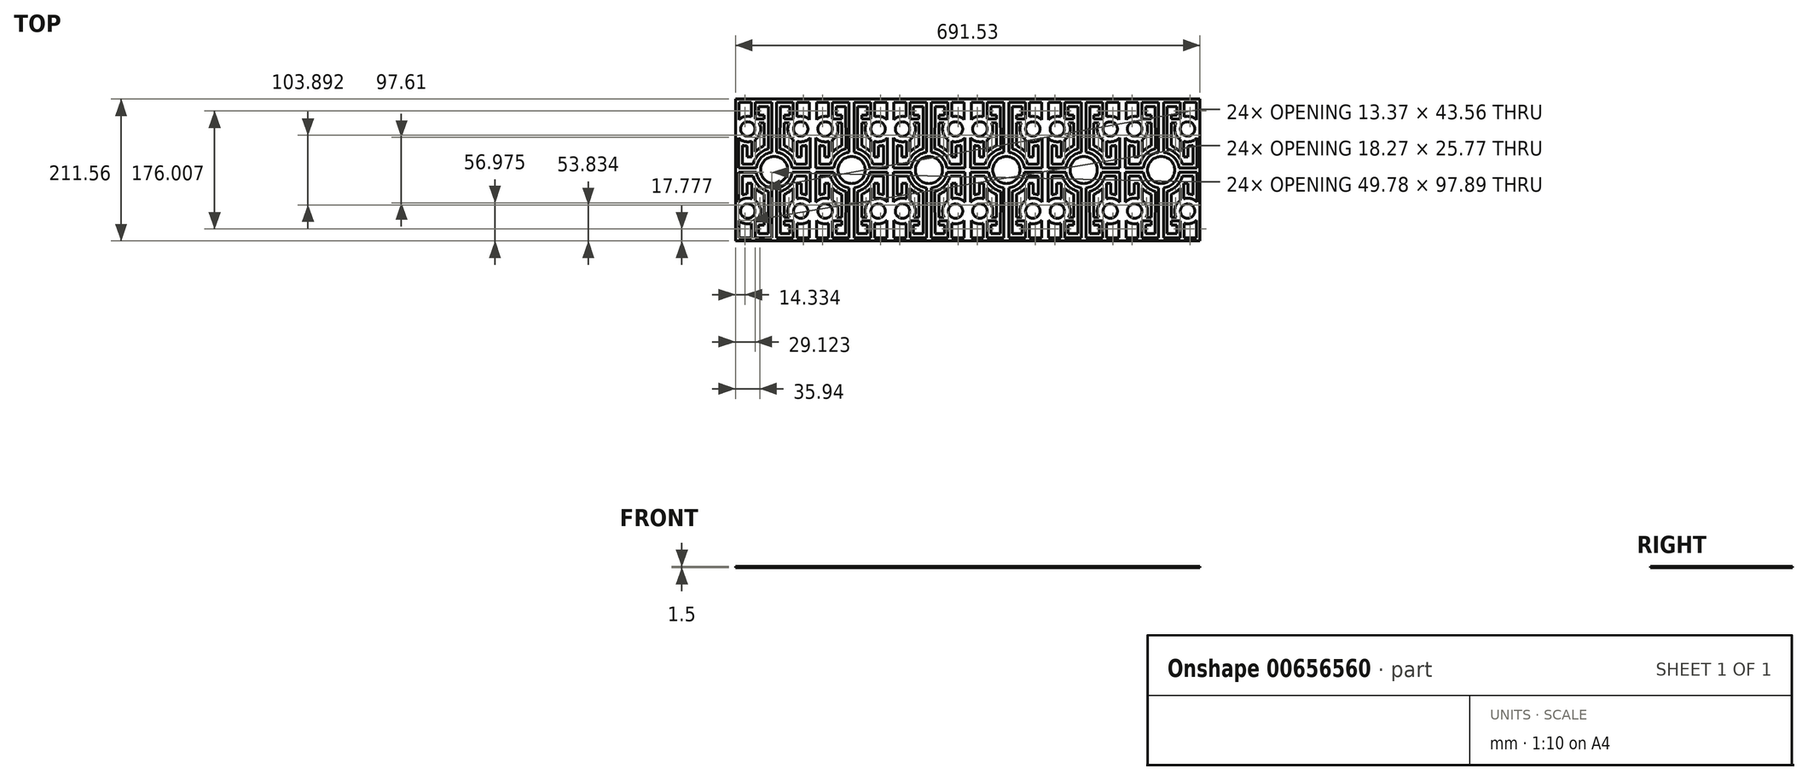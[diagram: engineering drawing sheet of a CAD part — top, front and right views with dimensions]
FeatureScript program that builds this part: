
annotation { "Feature Type Name" : "Feature", "Feature Type Description" : "" }
export const myFeature = defineFeature(function(context is Context, id is Id, definition is map)
    precondition{}
    {
        {
            var Q0;
            Q0=qCreatedBy(makeId("Top.planeOp"),FACE);
            var sketch = newSketch(context, id + "F0", { "sketchPlane" : qUnion([Q0])});
            skLineSegment(sketch, "E0.bottom", {"start": v(57.63, -105.78) * mm, "end": v(-57.63, -105.78) * mm});
            skLineSegment(sketch, "E0.top", {"start": v(57.63, 105.78) * mm, "end": v(-57.63, 105.78) * mm});
            skLineSegment(sketch, "E0.left", {"start": v(57.63, -105.78) * mm, "end": v(57.63, 105.78) * mm});
            skLineSegment(sketch, "E0.right", {"start": v(-57.63, -105.78) * mm, "end": v(-57.63, 105.78) * mm});
            skLineSegment(sketch, "E1.MirrorCS", {"start": v(-15, -75.88) * mm, "end": v(-15, -81.85) * mm});
            skLineSegment(sketch, "E2.MirrorCS", {"start": v(-40.17, -19.6) * mm, "end": v(-33.68, -19.6) * mm});
            skLineSegment(sketch, "E3.MirrorCS", {"start": v(-23.11, -81.85) * mm, "end": v(-15, -81.85) * mm});
            skArc(sketch, "E4.MirrorCS", {"start": v(-40.17, -35.72) * mm, "mid": v(-43.92, -36.1) * mm, "end": v(-47.58, -37.04) * mm});
            skLineSegment(sketch, "E5.MirrorCS", {"start": v(-23.1, -70.59) * mm, "end": v(-15, -70.59) * mm});
            skLineSegment(sketch, "E6.MirrorCS", {"start": v(-15, -75.88) * mm, "end": v(-28.38, -75.88) * mm});
            skLineSegment(sketch, "E7.MirrorCS", {"start": v(-28.38, -100.89) * mm, "end": v(-28.38, -75.88) * mm});
            skLineSegment(sketch, "E8.MirrorCS", {"start": v(-53.4, -47.98) * mm, "end": v(-53.4, -3) * mm});
            skLineSegment(sketch, "E9.MirrorCS", {"start": v(-47.58, -37.04) * mm, "end": v(-47.58, -8.78) * mm});
            skLineSegment(sketch, "E10.MirrorCS", {"start": v(-28.38, -100.89) * mm, "end": v(-3.61, -100.89) * mm});
            skLineSegment(sketch, "E11.MirrorCS", {"start": v(-15, -70.59) * mm, "end": v(-15, -36.2) * mm});
            skLineSegment(sketch, "E12.MirrorCS", {"start": v(-3.61, -26.62) * mm, "end": v(-3.61, -100.89) * mm});
            skLineSegment(sketch, "E13.MirrorCS", {"start": v(-57.63, 105.78) * mm, "end": v(-57.63, -105.78) * mm});
            skLineSegment(sketch, "E14.MirrorCS", {"start": v(57.63, 105.78) * mm, "end": v(57.63, -105.78) * mm});
            skLineSegment(sketch, "E15.MirrorCS", {"start": v(-28.37, -27.02) * mm, "end": v(-28.37, -45.33) * mm});
            skLineSegment(sketch, "E16.MirrorCS", {"start": v(-23.11, -81.85) * mm, "end": v(-23.11, -94.64) * mm});
            skLineSegment(sketch, "E17.MirrorCS", {"start": v(-23.11, -94.64) * mm, "end": v(-8.9, -94.64) * mm});
            skLineSegment(sketch, "E18.MirrorCS", {"start": v(-8.9, -94.64) * mm, "end": v(-8.67, -31.81) * mm});
            skLineSegment(sketch, "E19.MirrorCS", {"start": v(-34.16, -79.48) * mm, "end": v(-34.16, -100.89) * mm});
            skLineSegment(sketch, "E20.MirrorCS", {"start": v(-26.65, -3) * mm, "end": v(-53.4, -3) * mm});
            skArc(sketch, "E21.MirrorCS", {"start": v(-15, -36.2) * mm, "mid": v(-22.17, -32.32) * mm, "end": v(-28.37, -27.02) * mm});
            skArc(sketch, "E22.MirrorCS", {"start": v(-28.37, -45.33) * mm, "mid": v(-20.6, -56.84) * mm, "end": v(-22.52, -70.59) * mm});
            skArc(sketch, "E23.MirrorCS", {"start": v(-31.75, -8.78) * mm, "mid": v(-23.26, -23.35) * mm, "end": v(-8.67, -31.82) * mm});
            skLineSegment(sketch, "E24.MirrorCS", {"start": v(-33.68, -42.87) * mm, "end": v(-33.68, -19.6) * mm});
            skLineSegment(sketch, "E25.MirrorCS", {"start": v(-52.43, -100.89) * mm, "end": v(-34.16, -100.89) * mm});
            skLineSegment(sketch, "E26.MirrorCS", {"start": v(-52.43, -75.12) * mm, "end": v(-52.43, -100.89) * mm});
            skLineSegment(sketch, "E27.MirrorCS", {"start": v(-31.75, -8.78) * mm, "end": v(-47.58, -8.78) * mm});
            skArc(sketch, "E28.MirrorCS", {"start": v(-34.16, -79.48) * mm, "mid": v(-43.87, -79.71) * mm, "end": v(-52.43, -75.12) * mm});
            skArc(sketch, "E29.MirrorCS", {"start": v(-3.61, -26.62) * mm, "mid": v(-19.2, -18.77) * mm, "end": v(-26.65, -3) * mm});
            skCircle(sketch, "E30.MirrorC", {"center": v(-39.45, -61.2) * mm, "radius": 10.77 * mm});
            skArc(sketch, "E31.MirrorCS", {"start": v(-53.4, -47.98) * mm, "mid": v(-44.27, -42.6) * mm, "end": v(-33.68, -42.87) * mm});
            skLineSegment(sketch, "E32.MirrorCS", {"start": v(-40.17, -19.6) * mm, "end": v(-40.17, -35.72) * mm});
            skLineSegment(sketch, "E33.MirrorCS", {"start": v(-15, 75.88) * mm, "end": v(-15, 81.85) * mm});
            skLineSegment(sketch, "E34.MirrorCS", {"start": v(-40.17, 19.6) * mm, "end": v(-33.68, 19.6) * mm});
            skLineSegment(sketch, "E35.MirrorCS", {"start": v(-23.1, 70.59) * mm, "end": v(-15, 70.59) * mm});
            skArc(sketch, "E36.MirrorCS", {"start": v(-3.61, 26.62) * mm, "mid": v(-19.2, 18.77) * mm, "end": v(-26.65, 3) * mm});
            skLineSegment(sketch, "E37.MirrorCS", {"start": v(-8.9, 94.64) * mm, "end": v(-8.67, 31.81) * mm});
            skLineSegment(sketch, "E38.MirrorCS", {"start": v(-23.11, 81.85) * mm, "end": v(-15, 81.85) * mm});
            skLineSegment(sketch, "E39.MirrorCS", {"start": v(-15, 75.88) * mm, "end": v(-28.38, 75.88) * mm});
            skArc(sketch, "E40.MirrorCS", {"start": v(-28.37, 45.33) * mm, "mid": v(-20.6, 56.84) * mm, "end": v(-22.52, 70.59) * mm});
            skLineSegment(sketch, "E41.MirrorCS", {"start": v(-33.68, 42.87) * mm, "end": v(-33.68, 19.6) * mm});
            skArc(sketch, "E42.MirrorCS", {"start": v(-53.4, 47.98) * mm, "mid": v(-44.27, 42.6) * mm, "end": v(-33.68, 42.87) * mm});
            skLineSegment(sketch, "E43.MirrorCS", {"start": v(-31.75, 8.78) * mm, "end": v(-47.58, 8.78) * mm});
            skLineSegment(sketch, "E44.MirrorCS", {"start": v(-52.43, 100.89) * mm, "end": v(-34.16, 100.89) * mm});
            skArc(sketch, "E45.MirrorCS", {"start": v(-15, 36.2) * mm, "mid": v(-22.17, 32.32) * mm, "end": v(-28.37, 27.02) * mm});
            skLineSegment(sketch, "E46.MirrorCS", {"start": v(-28.37, 27.02) * mm, "end": v(-28.37, 45.33) * mm});
            skArc(sketch, "E47.MirrorCS", {"start": v(-31.75, 8.78) * mm, "mid": v(-23.26, 23.35) * mm, "end": v(-8.67, 31.82) * mm});
            skLineSegment(sketch, "E48.MirrorCS", {"start": v(-3.61, 26.62) * mm, "end": v(-3.61, 100.89) * mm});
            skArc(sketch, "E49.MirrorCS", {"start": v(-40.17, 35.72) * mm, "mid": v(-43.92, 36.1) * mm, "end": v(-47.58, 37.04) * mm});
            skArc(sketch, "E50.MirrorCS", {"start": v(-34.16, 79.48) * mm, "mid": v(-43.87, 79.71) * mm, "end": v(-52.43, 75.12) * mm});
            skLineSegment(sketch, "E51.MirrorCS", {"start": v(-28.38, 100.89) * mm, "end": v(-28.38, 75.88) * mm});
            skLineSegment(sketch, "E52.MirrorCS", {"start": v(-53.4, 47.98) * mm, "end": v(-53.4, 3) * mm});
            skLineSegment(sketch, "E53.MirrorCS", {"start": v(-47.58, 37.04) * mm, "end": v(-47.58, 8.78) * mm});
            skLineSegment(sketch, "E54.MirrorCS", {"start": v(-40.17, 19.6) * mm, "end": v(-40.17, 35.72) * mm});
            skLineSegment(sketch, "E55.MirrorCS", {"start": v(-34.16, 79.48) * mm, "end": v(-34.16, 100.89) * mm});
            skLineSegment(sketch, "E56.MirrorCS", {"start": v(-23.11, 81.85) * mm, "end": v(-23.11, 94.64) * mm});
            skLineSegment(sketch, "E57.MirrorCS", {"start": v(-26.65, 3) * mm, "end": v(-53.4, 3) * mm});
            skLineSegment(sketch, "E58.MirrorCS", {"start": v(-23.11, 94.64) * mm, "end": v(-8.9, 94.64) * mm});
            skLineSegment(sketch, "E59.MirrorCS", {"start": v(-52.43, 75.12) * mm, "end": v(-52.43, 100.89) * mm});
            skLineSegment(sketch, "E60.MirrorCS", {"start": v(-28.38, 100.89) * mm, "end": v(-3.61, 100.89) * mm});
            skLineSegment(sketch, "E61.MirrorCS", {"start": v(-15, 70.59) * mm, "end": v(-15, 36.2) * mm});
            skCircle(sketch, "E62.MirrorC", {"center": v(-39.45, 61.2) * mm, "radius": 10.77 * mm});
            skLineSegment(sketch, "E63.MirrorCS", {"start": v(-57.63, 105.78) * mm, "end": v(57.63, 105.78) * mm});
            skLineSegment(sketch, "E64.MirrorCS", {"start": v(-57.63, -105.78) * mm, "end": v(57.63, -105.78) * mm});
            skLineSegment(sketch, "E65.MirrorCS", {"start": v(23.1, -70.59) * mm, "end": v(15, -70.59) * mm});
            skLineSegment(sketch, "E66.MirrorCS", {"start": v(40.17, -19.6) * mm, "end": v(33.68, -19.6) * mm});
            skArc(sketch, "E67.MirrorCS", {"start": v(40.17, 35.72) * mm, "mid": v(43.92, 36.1) * mm, "end": v(47.58, 37.04) * mm});
            skLineSegment(sketch, "E68.MirrorCS", {"start": v(40.17, 19.6) * mm, "end": v(33.68, 19.6) * mm});
            skLineSegment(sketch, "E69.MirrorCS", {"start": v(15, -75.88) * mm, "end": v(15, -81.85) * mm});
            skLineSegment(sketch, "E70.MirrorCS", {"start": v(23.11, -81.85) * mm, "end": v(15, -81.85) * mm});
            skLineSegment(sketch, "E71.MirrorCS", {"start": v(23.11, 81.85) * mm, "end": v(15, 81.85) * mm});
            skLineSegment(sketch, "E72.MirrorCS", {"start": v(15, 75.88) * mm, "end": v(15, 81.85) * mm});
            skArc(sketch, "E73.MirrorCS", {"start": v(40.17, -35.72) * mm, "mid": v(43.92, -36.1) * mm, "end": v(47.58, -37.04) * mm});
            skLineSegment(sketch, "E74.MirrorCS", {"start": v(23.1, 70.59) * mm, "end": v(15, 70.59) * mm});
            skArc(sketch, "E75.MirrorCS", {"start": v(28.37, -45.33) * mm, "mid": v(20.6, -56.84) * mm, "end": v(22.52, -70.59) * mm});
            skLineSegment(sketch, "E76.MirrorCS", {"start": v(47.58, -37.04) * mm, "end": v(47.58, -8.78) * mm});
            skLineSegment(sketch, "E77.MirrorCS", {"start": v(40.17, -19.6) * mm, "end": v(40.17, -35.72) * mm});
            skLineSegment(sketch, "E78.MirrorCS", {"start": v(33.68, -42.87) * mm, "end": v(33.68, -19.6) * mm});
            skLineSegment(sketch, "E79.MirrorCS", {"start": v(31.75, 8.78) * mm, "end": v(47.58, 8.78) * mm});
            skArc(sketch, "E80.MirrorCS", {"start": v(28.37, 45.33) * mm, "mid": v(20.6, 56.84) * mm, "end": v(22.52, 70.59) * mm});
            skLineSegment(sketch, "E81.MirrorCS", {"start": v(28.38, -100.89) * mm, "end": v(3.61, -100.89) * mm});
            skLineSegment(sketch, "E82.MirrorCS", {"start": v(52.43, 100.89) * mm, "end": v(34.16, 100.89) * mm});
            skArc(sketch, "E83.MirrorCS", {"start": v(34.16, 79.48) * mm, "mid": v(43.87, 79.71) * mm, "end": v(52.43, 75.12) * mm});
            skArc(sketch, "E84.MirrorCS", {"start": v(31.75, -8.78) * mm, "mid": v(23.26, -23.35) * mm, "end": v(8.67, -31.82) * mm});
            skLineSegment(sketch, "E85.MirrorCS", {"start": v(31.75, -8.78) * mm, "end": v(47.58, -8.78) * mm});
            skLineSegment(sketch, "E86.MirrorCS", {"start": v(15, 70.59) * mm, "end": v(15, 36.2) * mm});
            skCircle(sketch, "E87.MirrorC", {"center": v(39.45, 61.2) * mm, "radius": 10.77 * mm});
            skLineSegment(sketch, "E88.MirrorCS", {"start": v(3.61, -26.62) * mm, "end": v(3.61, -100.89) * mm});
            skLineSegment(sketch, "E89.MirrorCS", {"start": v(52.43, 75.12) * mm, "end": v(52.43, 100.89) * mm});
            skArc(sketch, "E90.MirrorCS", {"start": v(53.4, 47.98) * mm, "mid": v(44.27, 42.6) * mm, "end": v(33.68, 42.87) * mm});
            skLineSegment(sketch, "E91.MirrorCS", {"start": v(28.37, -27.02) * mm, "end": v(28.37, -45.33) * mm});
            skLineSegment(sketch, "E92.MirrorCS", {"start": v(23.11, -81.85) * mm, "end": v(23.11, -94.64) * mm});
            skLineSegment(sketch, "E93.MirrorCS", {"start": v(47.58, 37.04) * mm, "end": v(47.58, 8.78) * mm});
            skArc(sketch, "E94.MirrorCS", {"start": v(53.4, -47.98) * mm, "mid": v(44.27, -42.6) * mm, "end": v(33.68, -42.87) * mm});
            skLineSegment(sketch, "E95.MirrorCS", {"start": v(34.16, 79.48) * mm, "end": v(34.16, 100.89) * mm});
            skLineSegment(sketch, "E96.MirrorCS", {"start": v(15, -75.88) * mm, "end": v(28.38, -75.88) * mm});
            skLineSegment(sketch, "E97.MirrorCS", {"start": v(28.38, 100.89) * mm, "end": v(3.61, 100.89) * mm});
            skLineSegment(sketch, "E98.MirrorCS", {"start": v(15, 75.88) * mm, "end": v(28.38, 75.88) * mm});
            skArc(sketch, "E99.MirrorCS", {"start": v(3.61, -26.62) * mm, "mid": v(19.2, -18.77) * mm, "end": v(26.65, -3) * mm});
            skLineSegment(sketch, "E100.MirrorCS", {"start": v(8.9, -94.64) * mm, "end": v(8.67, -31.81) * mm});
            skLineSegment(sketch, "E101.MirrorCS", {"start": v(52.43, -100.89) * mm, "end": v(34.16, -100.89) * mm});
            skLineSegment(sketch, "E102.MirrorCS", {"start": v(26.65, 3) * mm, "end": v(53.4, 3) * mm});
            skLineSegment(sketch, "E103.MirrorCS", {"start": v(34.16, -79.48) * mm, "end": v(34.16, -100.89) * mm});
            skArc(sketch, "E104.MirrorCS", {"start": v(3.61, 26.62) * mm, "mid": v(19.2, 18.77) * mm, "end": v(26.65, 3) * mm});
            skLineSegment(sketch, "E105.MirrorCS", {"start": v(23.11, -94.64) * mm, "end": v(8.9, -94.64) * mm});
            skLineSegment(sketch, "E106.MirrorCS", {"start": v(53.4, -47.98) * mm, "end": v(53.4, -3) * mm});
            skLineSegment(sketch, "E107.MirrorCS", {"start": v(8.9, 94.64) * mm, "end": v(8.67, 31.81) * mm});
            skLineSegment(sketch, "E108.MirrorCS", {"start": v(53.4, 47.98) * mm, "end": v(53.4, 3) * mm});
            skLineSegment(sketch, "E109.MirrorCS", {"start": v(26.65, -3) * mm, "end": v(53.4, -3) * mm});
            skLineSegment(sketch, "E110.MirrorCS", {"start": v(28.38, -100.89) * mm, "end": v(28.38, -75.88) * mm});
            skLineSegment(sketch, "E111.MirrorCS", {"start": v(52.43, -75.12) * mm, "end": v(52.43, -100.89) * mm});
            skCircle(sketch, "E112.MirrorC", {"center": v(39.45, -61.2) * mm, "radius": 10.77 * mm});
            skLineSegment(sketch, "E113.MirrorCS", {"start": v(23.11, 94.64) * mm, "end": v(8.9, 94.64) * mm});
            skLineSegment(sketch, "E114.MirrorCS", {"start": v(40.17, 19.6) * mm, "end": v(40.17, 35.72) * mm});
            skLineSegment(sketch, "E115.MirrorCS", {"start": v(33.68, 42.87) * mm, "end": v(33.68, 19.6) * mm});
            skLineSegment(sketch, "E116.MirrorCS", {"start": v(23.11, 81.85) * mm, "end": v(23.11, 94.64) * mm});
            skArc(sketch, "E117.MirrorCS", {"start": v(15, -36.2) * mm, "mid": v(22.17, -32.32) * mm, "end": v(28.37, -27.02) * mm});
            skLineSegment(sketch, "E118.MirrorCS", {"start": v(15, -70.59) * mm, "end": v(15, -36.2) * mm});
            skLineSegment(sketch, "E119.MirrorCS", {"start": v(3.61, 26.62) * mm, "end": v(3.61, 100.89) * mm});
            skArc(sketch, "E120.MirrorCS", {"start": v(34.16, -79.48) * mm, "mid": v(43.87, -79.71) * mm, "end": v(52.43, -75.12) * mm});
            skArc(sketch, "E121.MirrorCS", {"start": v(15, 36.2) * mm, "mid": v(22.17, 32.32) * mm, "end": v(28.37, 27.02) * mm});
            skLineSegment(sketch, "E122.MirrorCS", {"start": v(28.38, 100.89) * mm, "end": v(28.38, 75.88) * mm});
            skArc(sketch, "E123.MirrorCS", {"start": v(31.75, 8.78) * mm, "mid": v(23.26, 23.35) * mm, "end": v(8.67, 31.82) * mm});
            skLineSegment(sketch, "E124.MirrorCS", {"start": v(28.37, 27.02) * mm, "end": v(28.37, 45.33) * mm});
            skCircle(sketch, "E125", {"center": v(0, 0) * mm, "radius": 20.2 * mm});
            skLineSegment(sketch, "E126.MirrorCS", {"start": v(-172.88, 105.78) * mm, "end": v(-57.63, 105.78) * mm});
            skLineSegment(sketch, "E127.MirrorCS", {"start": v(-172.88, -105.78) * mm, "end": v(-172.88, 105.78) * mm});
            skLineSegment(sketch, "E128.MirrorCS", {"start": v(-57.63, -105.78) * mm, "end": v(-172.88, -105.78) * mm});
            skLineSegment(sketch, "E129.MirrorCS", {"start": v(-172.88, 105.78) * mm, "end": v(-172.88, -105.78) * mm});
            skLineSegment(sketch, "E130.MirrorCS", {"start": v(-57.63, 105.78) * mm, "end": v(-172.88, 105.78) * mm});
            skLineSegment(sketch, "E131.MirrorCS", {"start": v(-172.88, -105.78) * mm, "end": v(-57.63, -105.78) * mm});
            skArc(sketch, "E132.MirrorCS", {"start": v(-75.09, 35.72) * mm, "mid": v(-71.33, 36.1) * mm, "end": v(-67.67, 37.04) * mm});
            skLineSegment(sketch, "E133.MirrorCS", {"start": v(-75.09, 19.6) * mm, "end": v(-81.58, 19.6) * mm});
            skLineSegment(sketch, "E134.MirrorCS", {"start": v(-155.42, -19.6) * mm, "end": v(-148.93, -19.6) * mm});
            skLineSegment(sketch, "E135.MirrorCS", {"start": v(-92.16, 70.59) * mm, "end": v(-100.25, 70.59) * mm});
            skLineSegment(sketch, "E136.MirrorCS", {"start": v(-138.35, 70.59) * mm, "end": v(-130.26, 70.59) * mm});
            skArc(sketch, "E137.MirrorCS", {"start": v(-155.42, 35.72) * mm, "mid": v(-159.18, 36.1) * mm, "end": v(-162.84, 37.04) * mm});
            skLineSegment(sketch, "E138.MirrorCS", {"start": v(-138.35, -70.59) * mm, "end": v(-130.26, -70.59) * mm});
            skLineSegment(sketch, "E139.MirrorCS", {"start": v(-92.16, -70.59) * mm, "end": v(-100.25, -70.59) * mm});
            skLineSegment(sketch, "E140.MirrorCS", {"start": v(-100.25, 75.88) * mm, "end": v(-100.25, 81.85) * mm});
            skLineSegment(sketch, "E141.MirrorCS", {"start": v(-92.14, 81.85) * mm, "end": v(-100.25, 81.85) * mm});
            skArc(sketch, "E142.MirrorCS", {"start": v(-155.42, -35.72) * mm, "mid": v(-159.18, -36.1) * mm, "end": v(-162.84, -37.04) * mm});
            skLineSegment(sketch, "E143.MirrorCS", {"start": v(-92.14, -81.85) * mm, "end": v(-100.25, -81.85) * mm});
            skLineSegment(sketch, "E144.MirrorCS", {"start": v(-138.37, -81.85) * mm, "end": v(-130.26, -81.85) * mm});
            skLineSegment(sketch, "E145.MirrorCS", {"start": v(-100.25, -75.88) * mm, "end": v(-100.25, -81.85) * mm});
            skLineSegment(sketch, "E146.MirrorCS", {"start": v(-155.42, 19.6) * mm, "end": v(-148.93, 19.6) * mm});
            skLineSegment(sketch, "E147.MirrorCS", {"start": v(-130.26, -75.88) * mm, "end": v(-130.26, -81.85) * mm});
            skLineSegment(sketch, "E148.MirrorCS", {"start": v(-138.37, 81.85) * mm, "end": v(-130.26, 81.85) * mm});
            skLineSegment(sketch, "E149.MirrorCS", {"start": v(-130.26, 75.88) * mm, "end": v(-130.26, 81.85) * mm});
            skLineSegment(sketch, "E150.MirrorCS", {"start": v(-75.09, -19.6) * mm, "end": v(-81.58, -19.6) * mm});
            skArc(sketch, "E151.MirrorCS", {"start": v(-75.09, -35.72) * mm, "mid": v(-71.33, -36.1) * mm, "end": v(-67.67, -37.04) * mm});
            skLineSegment(sketch, "E152.MirrorCS", {"start": v(-81.58, -42.87) * mm, "end": v(-81.58, -19.6) * mm});
            skLineSegment(sketch, "E153.MirrorCS", {"start": v(-62.83, 75.12) * mm, "end": v(-62.83, 100.89) * mm});
            skLineSegment(sketch, "E154.MirrorCS", {"start": v(-106.35, -94.64) * mm, "end": v(-106.59, -31.81) * mm});
            skLineSegment(sketch, "E155.MirrorCS", {"start": v(-67.67, -37.04) * mm, "end": v(-67.67, -8.78) * mm});
            skArc(sketch, "E156.MirrorCS", {"start": v(-147, -8.78) * mm, "mid": v(-138.51, -23.35) * mm, "end": v(-123.92, -31.82) * mm});
            skLineSegment(sketch, "E157.MirrorCS", {"start": v(-141.9, 3) * mm, "end": v(-168.65, 3) * mm});
            skLineSegment(sketch, "E158.MirrorCS", {"start": v(-130.26, 75.88) * mm, "end": v(-143.64, 75.88) * mm});
            skLineSegment(sketch, "E159.MirrorCS", {"start": v(-124.16, -94.64) * mm, "end": v(-123.92, -31.81) * mm});
            skLineSegment(sketch, "E160.MirrorCS", {"start": v(-118.87, -26.62) * mm, "end": v(-118.87, -100.89) * mm});
            skArc(sketch, "E161.MirrorCS", {"start": v(-130.26, 36.2) * mm, "mid": v(-137.42, 32.32) * mm, "end": v(-143.63, 27.02) * mm});
            skArc(sketch, "E162.MirrorCS", {"start": v(-81.1, 79.48) * mm, "mid": v(-71.39, 79.71) * mm, "end": v(-62.83, 75.12) * mm});
            skLineSegment(sketch, "E163.MirrorCS", {"start": v(-62.83, -100.89) * mm, "end": v(-81.1, -100.89) * mm});
            skLineSegment(sketch, "E164.MirrorCS", {"start": v(-86.87, 100.89) * mm, "end": v(-111.64, 100.89) * mm});
            skLineSegment(sketch, "E165.MirrorCS", {"start": v(-86.87, -100.89) * mm, "end": v(-111.64, -100.89) * mm});
            skLineSegment(sketch, "E166.MirrorCS", {"start": v(-147, -8.78) * mm, "end": v(-162.84, -8.78) * mm});
            skLineSegment(sketch, "E167.MirrorCS", {"start": v(-143.64, 100.89) * mm, "end": v(-143.64, 75.88) * mm});
            skLineSegment(sketch, "E168.MirrorCS", {"start": v(-143.64, -100.89) * mm, "end": v(-118.87, -100.89) * mm});
            skLineSegment(sketch, "E169.MirrorCS", {"start": v(-138.37, 81.85) * mm, "end": v(-138.37, 94.64) * mm});
            skLineSegment(sketch, "E170.MirrorCS", {"start": v(-167.68, -100.89) * mm, "end": v(-149.4, -100.89) * mm});
            skLineSegment(sketch, "E171.MirrorCS", {"start": v(-138.37, -81.85) * mm, "end": v(-138.37, -94.64) * mm});
            skArc(sketch, "E172.MirrorCS", {"start": v(-143.63, 45.33) * mm, "mid": v(-135.85, 56.84) * mm, "end": v(-137.77, 70.59) * mm});
            skLineSegment(sketch, "E173.MirrorCS", {"start": v(-86.87, 100.89) * mm, "end": v(-86.87, 75.88) * mm});
            skLineSegment(sketch, "E174.MirrorCS", {"start": v(-62.83, -75.12) * mm, "end": v(-62.83, -100.89) * mm});
            skArc(sketch, "E175.MirrorCS", {"start": v(-61.86, 47.98) * mm, "mid": v(-70.99, 42.6) * mm, "end": v(-81.58, 42.87) * mm});
            skArc(sketch, "E176.MirrorCS", {"start": v(-86.88, 45.33) * mm, "mid": v(-94.66, 56.84) * mm, "end": v(-92.74, 70.59) * mm});
            skLineSegment(sketch, "E177.MirrorCS", {"start": v(-88.6, 3) * mm, "end": v(-61.86, 3) * mm});
            skLineSegment(sketch, "E178.MirrorCS", {"start": v(-130.26, 70.59) * mm, "end": v(-130.26, 36.2) * mm});
            skLineSegment(sketch, "E179.MirrorCS", {"start": v(-147, 8.78) * mm, "end": v(-162.84, 8.78) * mm});
            skCircle(sketch, "E180.MirrorC", {"center": v(-154.7, -61.2) * mm, "radius": 10.77 * mm});
            skArc(sketch, "E181.MirrorCS", {"start": v(-130.26, -36.2) * mm, "mid": v(-137.42, -32.32) * mm, "end": v(-143.63, -27.02) * mm});
            skArc(sketch, "E182.MirrorCS", {"start": v(-168.65, -47.98) * mm, "mid": v(-159.52, -42.6) * mm, "end": v(-148.93, -42.87) * mm});
            skArc(sketch, "E183.MirrorCS", {"start": v(-168.65, 47.98) * mm, "mid": v(-159.52, 42.6) * mm, "end": v(-148.93, 42.87) * mm});
            skLineSegment(sketch, "E184.MirrorCS", {"start": v(-67.67, 37.04) * mm, "end": v(-67.67, 8.78) * mm});
            skArc(sketch, "E185.MirrorCS", {"start": v(-83.5, -8.78) * mm, "mid": v(-92, -23.35) * mm, "end": v(-106.59, -31.82) * mm});
            skCircle(sketch, "E186.MirrorC", {"center": v(-154.7, 61.2) * mm, "radius": 10.77 * mm});
            skLineSegment(sketch, "E187.MirrorCS", {"start": v(-138.37, 94.64) * mm, "end": v(-124.16, 94.64) * mm});
            skLineSegment(sketch, "E188.MirrorCS", {"start": v(-149.4, -79.48) * mm, "end": v(-149.4, -100.89) * mm});
            skLineSegment(sketch, "E189.MirrorCS", {"start": v(-167.68, -75.12) * mm, "end": v(-167.68, -100.89) * mm});
            skArc(sketch, "E190.MirrorCS", {"start": v(-111.64, 26.62) * mm, "mid": v(-96.06, 18.77) * mm, "end": v(-88.6, 3) * mm});
            skLineSegment(sketch, "E191.MirrorCS", {"start": v(-83.5, -8.78) * mm, "end": v(-67.67, -8.78) * mm});
            skArc(sketch, "E192.MirrorCS", {"start": v(-149.4, 79.48) * mm, "mid": v(-159.12, 79.71) * mm, "end": v(-167.68, 75.12) * mm});
            skArc(sketch, "E193.MirrorCS", {"start": v(-118.87, 26.62) * mm, "mid": v(-134.45, 18.77) * mm, "end": v(-141.9, 3) * mm});
            skLineSegment(sketch, "E194.MirrorCS", {"start": v(-155.42, 19.6) * mm, "end": v(-155.42, 35.72) * mm});
            skLineSegment(sketch, "E195.MirrorCS", {"start": v(-61.86, 47.98) * mm, "end": v(-61.86, 3) * mm});
            skLineSegment(sketch, "E196.MirrorCS", {"start": v(-106.35, 94.64) * mm, "end": v(-106.59, 31.81) * mm});
            skArc(sketch, "E197.MirrorCS", {"start": v(-81.1, -79.48) * mm, "mid": v(-71.39, -79.71) * mm, "end": v(-62.83, -75.12) * mm});
            skArc(sketch, "E198.MirrorCS", {"start": v(-86.88, -45.33) * mm, "mid": v(-94.66, -56.84) * mm, "end": v(-92.74, -70.59) * mm});
            skLineSegment(sketch, "E199.MirrorCS", {"start": v(-86.88, 27.02) * mm, "end": v(-86.88, 45.33) * mm});
            skArc(sketch, "E200.MirrorCS", {"start": v(-100.25, -36.2) * mm, "mid": v(-93.09, -32.32) * mm, "end": v(-86.88, -27.02) * mm});
            skLineSegment(sketch, "E201.MirrorCS", {"start": v(-148.93, -42.87) * mm, "end": v(-148.93, -19.6) * mm});
            skLineSegment(sketch, "E202.MirrorCS", {"start": v(-143.64, 100.89) * mm, "end": v(-118.87, 100.89) * mm});
            skLineSegment(sketch, "E203.MirrorCS", {"start": v(-130.26, -70.59) * mm, "end": v(-130.26, -36.2) * mm});
            skLineSegment(sketch, "E204.MirrorCS", {"start": v(-138.37, -94.64) * mm, "end": v(-124.16, -94.64) * mm});
            skArc(sketch, "E205.MirrorCS", {"start": v(-111.64, -26.62) * mm, "mid": v(-96.06, -18.77) * mm, "end": v(-88.6, -3) * mm});
            skLineSegment(sketch, "E206.MirrorCS", {"start": v(-81.1, -79.48) * mm, "end": v(-81.1, -100.89) * mm});
            skArc(sketch, "E207.MirrorCS", {"start": v(-100.25, 36.2) * mm, "mid": v(-93.09, 32.32) * mm, "end": v(-86.88, 27.02) * mm});
            skLineSegment(sketch, "E208.MirrorCS", {"start": v(-92.14, -81.85) * mm, "end": v(-92.14, -94.64) * mm});
            skArc(sketch, "E209.MirrorCS", {"start": v(-61.86, -47.98) * mm, "mid": v(-70.99, -42.6) * mm, "end": v(-81.58, -42.87) * mm});
            skLineSegment(sketch, "E210.MirrorCS", {"start": v(-167.68, 75.12) * mm, "end": v(-167.68, 100.89) * mm});
            skLineSegment(sketch, "E211.MirrorCS", {"start": v(-168.65, 47.98) * mm, "end": v(-168.65, 3) * mm});
            skLineSegment(sketch, "E212.MirrorCS", {"start": v(-86.88, -27.02) * mm, "end": v(-86.88, -45.33) * mm});
            skLineSegment(sketch, "E213.MirrorCS", {"start": v(-75.09, 19.6) * mm, "end": v(-75.09, 35.72) * mm});
            skLineSegment(sketch, "E214.MirrorCS", {"start": v(-100.25, 75.88) * mm, "end": v(-86.87, 75.88) * mm});
            skCircle(sketch, "E215.MirrorC", {"center": v(-75.8, -61.2) * mm, "radius": 10.77 * mm});
            skLineSegment(sketch, "E216.MirrorCS", {"start": v(-111.64, 26.62) * mm, "end": v(-111.64, 100.89) * mm});
            skLineSegment(sketch, "E217.MirrorCS", {"start": v(-100.25, -70.59) * mm, "end": v(-100.25, -36.2) * mm});
            skLineSegment(sketch, "E218.MirrorCS", {"start": v(-143.63, -27.02) * mm, "end": v(-143.63, -45.33) * mm});
            skLineSegment(sketch, "E219.MirrorCS", {"start": v(-118.87, 26.62) * mm, "end": v(-118.87, 100.89) * mm});
            skLineSegment(sketch, "E220.MirrorCS", {"start": v(-168.65, -47.98) * mm, "end": v(-168.65, -3) * mm});
            skLineSegment(sketch, "E221.MirrorCS", {"start": v(-81.1, 79.48) * mm, "end": v(-81.1, 100.89) * mm});
            skLineSegment(sketch, "E222.MirrorCS", {"start": v(-83.5, 8.78) * mm, "end": v(-67.67, 8.78) * mm});
            skLineSegment(sketch, "E223.MirrorCS", {"start": v(-111.64, -26.62) * mm, "end": v(-111.64, -100.89) * mm});
            skArc(sketch, "E224.MirrorCS", {"start": v(-143.63, -45.33) * mm, "mid": v(-135.85, -56.84) * mm, "end": v(-137.77, -70.59) * mm});
            skArc(sketch, "E225.MirrorCS", {"start": v(-149.4, -79.48) * mm, "mid": v(-159.12, -79.71) * mm, "end": v(-167.68, -75.12) * mm});
            skLineSegment(sketch, "E226.MirrorCS", {"start": v(-124.16, 94.64) * mm, "end": v(-123.92, 31.81) * mm});
            skLineSegment(sketch, "E227.MirrorCS", {"start": v(-92.14, 81.85) * mm, "end": v(-92.14, 94.64) * mm});
            skLineSegment(sketch, "E228.MirrorCS", {"start": v(-81.58, 42.87) * mm, "end": v(-81.58, 19.6) * mm});
            skLineSegment(sketch, "E229.MirrorCS", {"start": v(-75.09, -19.6) * mm, "end": v(-75.09, -35.72) * mm});
            skLineSegment(sketch, "E230.MirrorCS", {"start": v(-92.14, 94.64) * mm, "end": v(-106.35, 94.64) * mm});
            skLineSegment(sketch, "E231.MirrorCS", {"start": v(-162.84, -37.04) * mm, "end": v(-162.84, -8.78) * mm});
            skLineSegment(sketch, "E232.MirrorCS", {"start": v(-167.68, 100.89) * mm, "end": v(-149.4, 100.89) * mm});
            skLineSegment(sketch, "E233.MirrorCS", {"start": v(-92.14, -94.64) * mm, "end": v(-106.35, -94.64) * mm});
            skArc(sketch, "E234.MirrorCS", {"start": v(-83.5, 8.78) * mm, "mid": v(-92, 23.35) * mm, "end": v(-106.59, 31.82) * mm});
            skLineSegment(sketch, "E235.MirrorCS", {"start": v(-162.84, 37.04) * mm, "end": v(-162.84, 8.78) * mm});
            skLineSegment(sketch, "E236.MirrorCS", {"start": v(-155.42, -19.6) * mm, "end": v(-155.42, -35.72) * mm});
            skLineSegment(sketch, "E237.MirrorCS", {"start": v(-141.9, -3) * mm, "end": v(-168.65, -3) * mm});
            skLineSegment(sketch, "E238.MirrorCS", {"start": v(-61.86, -47.98) * mm, "end": v(-61.86, -3) * mm});
            skArc(sketch, "E239.MirrorCS", {"start": v(-147, 8.78) * mm, "mid": v(-138.51, 23.35) * mm, "end": v(-123.92, 31.82) * mm});
            skLineSegment(sketch, "E240.MirrorCS", {"start": v(-143.64, -100.89) * mm, "end": v(-143.64, -75.88) * mm});
            skLineSegment(sketch, "E241.MirrorCS", {"start": v(-143.63, 27.02) * mm, "end": v(-143.63, 45.33) * mm});
            skLineSegment(sketch, "E242.MirrorCS", {"start": v(-62.83, 100.89) * mm, "end": v(-81.1, 100.89) * mm});
            skLineSegment(sketch, "E243.MirrorCS", {"start": v(-100.25, 70.59) * mm, "end": v(-100.25, 36.2) * mm});
            skLineSegment(sketch, "E244.MirrorCS", {"start": v(-86.87, -100.89) * mm, "end": v(-86.87, -75.88) * mm});
            skLineSegment(sketch, "E245.MirrorCS", {"start": v(-149.4, 79.48) * mm, "end": v(-149.4, 100.89) * mm});
            skLineSegment(sketch, "E246.MirrorCS", {"start": v(-88.6, -3) * mm, "end": v(-61.86, -3) * mm});
            skLineSegment(sketch, "E247.MirrorCS", {"start": v(-100.25, -75.88) * mm, "end": v(-86.87, -75.88) * mm});
            skLineSegment(sketch, "E248.MirrorCS", {"start": v(-130.26, -75.88) * mm, "end": v(-143.64, -75.88) * mm});
            skLineSegment(sketch, "E249.MirrorCS", {"start": v(-148.93, 42.87) * mm, "end": v(-148.93, 19.6) * mm});
            skCircle(sketch, "E250.MirrorC", {"center": v(-75.8, 61.2) * mm, "radius": 10.77 * mm});
            skArc(sketch, "E251.MirrorCS", {"start": v(-118.87, -26.62) * mm, "mid": v(-134.45, -18.77) * mm, "end": v(-141.9, -3) * mm});
            skCircle(sketch, "E252.MirrorC", {"center": v(-115.25, 0) * mm, "radius": 20.2 * mm});
            skLineSegment(sketch, "E253.MirrorCS", {"start": v(172.88, 105.78) * mm, "end": v(172.88, -105.78) * mm});
            skLineSegment(sketch, "E254.MirrorCS", {"start": v(172.88, -105.78) * mm, "end": v(172.88, 105.78) * mm});
            skLineSegment(sketch, "E255.MirrorCS", {"start": v(172.88, 105.78) * mm, "end": v(288.14, 105.78) * mm});
            skLineSegment(sketch, "E256.MirrorCS", {"start": v(57.63, 105.78) * mm, "end": v(172.88, 105.78) * mm});
            skLineSegment(sketch, "E257.MirrorCS", {"start": v(172.88, -105.78) * mm, "end": v(57.63, -105.78) * mm});
            skLineSegment(sketch, "E258.MirrorCS", {"start": v(172.88, -105.78) * mm, "end": v(288.14, -105.78) * mm});
            skLineSegment(sketch, "E259.MirrorCS", {"start": v(288.14, -105.78) * mm, "end": v(288.14, 105.78) * mm});
            skLineSegment(sketch, "E260.MirrorCS", {"start": v(288.14, 105.78) * mm, "end": v(172.88, 105.78) * mm});
            skLineSegment(sketch, "E261.MirrorCS", {"start": v(288.14, 105.78) * mm, "end": v(288.14, -105.78) * mm});
            skLineSegment(sketch, "E262.MirrorCS", {"start": v(172.88, 105.78) * mm, "end": v(57.63, 105.78) * mm});
            skLineSegment(sketch, "E263.MirrorCS", {"start": v(57.63, -105.78) * mm, "end": v(172.88, -105.78) * mm});
            skLineSegment(sketch, "E264.MirrorCS", {"start": v(288.14, -105.78) * mm, "end": v(172.88, -105.78) * mm});
            skLineSegment(sketch, "E265.MirrorCS", {"start": v(215.5, 75.88) * mm, "end": v(215.5, 81.85) * mm});
            skLineSegment(sketch, "E266.MirrorCS", {"start": v(130.26, 75.88) * mm, "end": v(130.26, 81.85) * mm});
            skLineSegment(sketch, "E267.MirrorCS", {"start": v(130.26, -75.88) * mm, "end": v(130.26, -81.85) * mm});
            skLineSegment(sketch, "E268.MirrorCS", {"start": v(100.25, -75.88) * mm, "end": v(100.25, -81.85) * mm});
            skLineSegment(sketch, "E269.MirrorCS", {"start": v(245.5, 75.88) * mm, "end": v(245.5, 81.85) * mm});
            skLineSegment(sketch, "E270.MirrorCS", {"start": v(253.6, 70.59) * mm, "end": v(245.5, 70.59) * mm});
            skLineSegment(sketch, "E271.MirrorCS", {"start": v(215.5, -75.88) * mm, "end": v(202.13, -75.88) * mm});
            skArc(sketch, "E272.MirrorCS", {"start": v(155.42, 35.72) * mm, "mid": v(159.18, 36.1) * mm, "end": v(162.84, 37.04) * mm});
            skLineSegment(sketch, "E273.MirrorCS", {"start": v(155.42, 19.6) * mm, "end": v(148.93, 19.6) * mm});
            skLineSegment(sketch, "E274.MirrorCS", {"start": v(75.09, -19.6) * mm, "end": v(81.58, -19.6) * mm});
            skLineSegment(sketch, "E275.MirrorCS", {"start": v(100.25, 75.88) * mm, "end": v(86.87, 75.88) * mm});
            skLineSegment(sketch, "E276.MirrorCS", {"start": v(138.35, 70.59) * mm, "end": v(130.26, 70.59) * mm});
            skLineSegment(sketch, "E277.MirrorCS", {"start": v(92.16, 70.59) * mm, "end": v(100.25, 70.59) * mm});
            skArc(sketch, "E278.MirrorCS", {"start": v(270.68, 35.72) * mm, "mid": v(274.43, 36.1) * mm, "end": v(278.1, 37.04) * mm});
            skLineSegment(sketch, "E279.MirrorCS", {"start": v(215.5, 75.88) * mm, "end": v(202.13, 75.88) * mm});
            skLineSegment(sketch, "E280.MirrorCS", {"start": v(253.6, -70.59) * mm, "end": v(245.5, -70.59) * mm});
            skLineSegment(sketch, "E281.MirrorCS", {"start": v(190.34, -19.6) * mm, "end": v(196.83, -19.6) * mm});
            skArc(sketch, "E282.MirrorCS", {"start": v(190.34, -35.72) * mm, "mid": v(186.59, -36.1) * mm, "end": v(182.93, -37.04) * mm});
            skLineSegment(sketch, "E283.MirrorCS", {"start": v(207.42, -70.59) * mm, "end": v(215.5, -70.59) * mm});
            skLineSegment(sketch, "E284.MirrorCS", {"start": v(92.16, -70.59) * mm, "end": v(100.25, -70.59) * mm});
            skLineSegment(sketch, "E285.MirrorCS", {"start": v(253.62, 81.85) * mm, "end": v(245.5, 81.85) * mm});
            skLineSegment(sketch, "E286.MirrorCS", {"start": v(207.42, 70.59) * mm, "end": v(215.5, 70.59) * mm});
            skLineSegment(sketch, "E287.MirrorCS", {"start": v(138.35, -70.59) * mm, "end": v(130.26, -70.59) * mm});
            skArc(sketch, "E288.MirrorCS", {"start": v(270.68, -35.72) * mm, "mid": v(274.43, -36.1) * mm, "end": v(278.1, -37.04) * mm});
            skLineSegment(sketch, "E289.MirrorCS", {"start": v(207.4, 81.85) * mm, "end": v(215.5, 81.85) * mm});
            skLineSegment(sketch, "E290.MirrorCS", {"start": v(138.37, 81.85) * mm, "end": v(130.26, 81.85) * mm});
            skArc(sketch, "E291.MirrorCS", {"start": v(75.09, -35.72) * mm, "mid": v(71.33, -36.1) * mm, "end": v(67.67, -37.04) * mm});
            skLineSegment(sketch, "E292.MirrorCS", {"start": v(270.68, -19.6) * mm, "end": v(264.19, -19.6) * mm});
            skLineSegment(sketch, "E293.MirrorCS", {"start": v(138.37, -81.85) * mm, "end": v(130.26, -81.85) * mm});
            skLineSegment(sketch, "E294.MirrorCS", {"start": v(130.26, 75.88) * mm, "end": v(143.64, 75.88) * mm});
            skLineSegment(sketch, "E295.MirrorCS", {"start": v(92.14, -81.85) * mm, "end": v(100.25, -81.85) * mm});
            skLineSegment(sketch, "E296.MirrorCS", {"start": v(215.5, -75.88) * mm, "end": v(215.5, -81.85) * mm});
            skLineSegment(sketch, "E297.MirrorCS", {"start": v(207.4, -81.85) * mm, "end": v(215.5, -81.85) * mm});
            skLineSegment(sketch, "E298.MirrorCS", {"start": v(75.09, 19.6) * mm, "end": v(81.58, 19.6) * mm});
            skLineSegment(sketch, "E299.MirrorCS", {"start": v(190.34, 19.6) * mm, "end": v(196.83, 19.6) * mm});
            skLineSegment(sketch, "E300.MirrorCS", {"start": v(253.62, -81.85) * mm, "end": v(245.5, -81.85) * mm});
            skLineSegment(sketch, "E301.MirrorCS", {"start": v(270.68, 19.6) * mm, "end": v(264.19, 19.6) * mm});
            skLineSegment(sketch, "E302.MirrorCS", {"start": v(245.5, -75.88) * mm, "end": v(258.9, -75.88) * mm});
            skArc(sketch, "E303.MirrorCS", {"start": v(75.09, 35.72) * mm, "mid": v(71.33, 36.1) * mm, "end": v(67.67, 37.04) * mm});
            skLineSegment(sketch, "E304.MirrorCS", {"start": v(245.5, 75.88) * mm, "end": v(258.9, 75.88) * mm});
            skLineSegment(sketch, "E305.MirrorCS", {"start": v(92.14, 81.85) * mm, "end": v(100.25, 81.85) * mm});
            skLineSegment(sketch, "E306.MirrorCS", {"start": v(245.5, -75.88) * mm, "end": v(245.5, -81.85) * mm});
            skLineSegment(sketch, "E307.MirrorCS", {"start": v(100.25, 75.88) * mm, "end": v(100.25, 81.85) * mm});
            skLineSegment(sketch, "E308.MirrorCS", {"start": v(130.26, -75.88) * mm, "end": v(143.64, -75.88) * mm});
            skLineSegment(sketch, "E309.MirrorCS", {"start": v(100.25, -75.88) * mm, "end": v(86.87, -75.88) * mm});
            skArc(sketch, "E310.MirrorCS", {"start": v(190.34, 35.72) * mm, "mid": v(186.59, 36.1) * mm, "end": v(182.93, 37.04) * mm});
            skLineSegment(sketch, "E311.MirrorCS", {"start": v(155.42, -19.6) * mm, "end": v(148.93, -19.6) * mm});
            skArc(sketch, "E312.MirrorCS", {"start": v(155.42, -35.72) * mm, "mid": v(159.18, -36.1) * mm, "end": v(162.84, -37.04) * mm});
            skLineSegment(sketch, "E313.MirrorCS", {"start": v(202.13, 100.89) * mm, "end": v(226.9, 100.89) * mm});
            skCircle(sketch, "E314.MirrorC", {"center": v(269.96, -61.2) * mm, "radius": 10.77 * mm});
            skLineSegment(sketch, "E315.MirrorCS", {"start": v(196.83, 42.87) * mm, "end": v(196.83, 19.6) * mm});
            skLineSegment(sketch, "E316.MirrorCS", {"start": v(202.13, -100.89) * mm, "end": v(202.13, -75.88) * mm});
            skLineSegment(sketch, "E317.MirrorCS", {"start": v(221.6, 94.64) * mm, "end": v(221.84, 31.81) * mm});
            skLineSegment(sketch, "E318.MirrorCS", {"start": v(202.14, -27.02) * mm, "end": v(202.14, -45.33) * mm});
            skLineSegment(sketch, "E319.MirrorCS", {"start": v(178.08, -100.89) * mm, "end": v(196.35, -100.89) * mm});
            skArc(sketch, "E320.MirrorCS", {"start": v(215.5, 36.2) * mm, "mid": v(208.34, 32.32) * mm, "end": v(202.14, 27.02) * mm});
            skLineSegment(sketch, "E321.MirrorCS", {"start": v(282.94, -100.89) * mm, "end": v(264.66, -100.89) * mm});
            skLineSegment(sketch, "E322.MirrorCS", {"start": v(196.35, 79.48) * mm, "end": v(196.35, 100.89) * mm});
            skArc(sketch, "E323.MirrorCS", {"start": v(198.76, -8.78) * mm, "mid": v(207.25, -23.35) * mm, "end": v(221.84, -31.82) * mm});
            skLineSegment(sketch, "E324.MirrorCS", {"start": v(278.1, 37.04) * mm, "end": v(278.1, 8.78) * mm});
            skLineSegment(sketch, "E325.MirrorCS", {"start": v(148.93, -42.87) * mm, "end": v(148.93, -19.6) * mm});
            skLineSegment(sketch, "E326.MirrorCS", {"start": v(124.16, -94.64) * mm, "end": v(123.92, -31.81) * mm});
            skLineSegment(sketch, "E327.MirrorCS", {"start": v(167.68, 75.12) * mm, "end": v(167.68, 100.89) * mm});
            skLineSegment(sketch, "E328.MirrorCS", {"start": v(162.84, -37.04) * mm, "end": v(162.84, -8.78) * mm});
            skArc(sketch, "E329.MirrorCS", {"start": v(83.5, -8.78) * mm, "mid": v(92, -23.35) * mm, "end": v(106.59, -31.82) * mm});
            skLineSegment(sketch, "E330.MirrorCS", {"start": v(88.6, 3) * mm, "end": v(61.86, 3) * mm});
            skLineSegment(sketch, "E331.MirrorCS", {"start": v(106.35, -94.64) * mm, "end": v(106.59, -31.81) * mm});
            skArc(sketch, "E332.MirrorCS", {"start": v(100.25, 36.2) * mm, "mid": v(93.09, 32.32) * mm, "end": v(86.88, 27.02) * mm});
            skLineSegment(sketch, "E333.MirrorCS", {"start": v(111.64, -26.62) * mm, "end": v(111.64, -100.89) * mm});
            skLineSegment(sketch, "E334.MirrorCS", {"start": v(202.13, -100.89) * mm, "end": v(226.9, -100.89) * mm});
            skArc(sketch, "E335.MirrorCS", {"start": v(245.5, -36.2) * mm, "mid": v(252.68, -32.32) * mm, "end": v(258.88, -27.02) * mm});
            skLineSegment(sketch, "E336.MirrorCS", {"start": v(264.66, 79.48) * mm, "end": v(264.66, 100.89) * mm});
            skLineSegment(sketch, "E337.MirrorCS", {"start": v(190.34, -19.6) * mm, "end": v(190.34, -35.72) * mm});
            skLineSegment(sketch, "E338.MirrorCS", {"start": v(190.34, 19.6) * mm, "end": v(190.34, 35.72) * mm});
            skArc(sketch, "E339.MirrorCS", {"start": v(196.35, -79.48) * mm, "mid": v(186.64, -79.71) * mm, "end": v(178.08, -75.12) * mm});
            skLineSegment(sketch, "E340.MirrorCS", {"start": v(253.62, -81.85) * mm, "end": v(253.62, -94.64) * mm});
            skLineSegment(sketch, "E341.MirrorCS", {"start": v(182.93, 37.04) * mm, "end": v(182.93, 8.78) * mm});
            skLineSegment(sketch, "E342.MirrorCS", {"start": v(207.4, -94.64) * mm, "end": v(221.6, -94.64) * mm});
            skArc(sketch, "E343.MirrorCS", {"start": v(234.12, 26.62) * mm, "mid": v(249.7, 18.77) * mm, "end": v(257.16, 3) * mm});
            skArc(sketch, "E344.MirrorCS", {"start": v(149.4, 79.48) * mm, "mid": v(159.12, 79.71) * mm, "end": v(167.68, 75.12) * mm});
            skLineSegment(sketch, "E345.MirrorCS", {"start": v(167.68, -100.89) * mm, "end": v(149.4, -100.89) * mm});
            skLineSegment(sketch, "E346.MirrorCS", {"start": v(143.64, 100.89) * mm, "end": v(118.87, 100.89) * mm});
            skLineSegment(sketch, "E347.MirrorCS", {"start": v(143.64, -100.89) * mm, "end": v(118.87, -100.89) * mm});
            skLineSegment(sketch, "E348.MirrorCS", {"start": v(83.5, -8.78) * mm, "end": v(67.67, -8.78) * mm});
            skLineSegment(sketch, "E349.MirrorCS", {"start": v(86.87, 100.89) * mm, "end": v(86.87, 75.88) * mm});
            skLineSegment(sketch, "E350.MirrorCS", {"start": v(86.87, -100.89) * mm, "end": v(111.64, -100.89) * mm});
            skLineSegment(sketch, "E351.MirrorCS", {"start": v(92.14, 81.85) * mm, "end": v(92.14, 94.64) * mm});
            skLineSegment(sketch, "E352.MirrorCS", {"start": v(62.83, -100.89) * mm, "end": v(81.1, -100.89) * mm});
            skLineSegment(sketch, "E353.MirrorCS", {"start": v(92.14, -81.85) * mm, "end": v(92.14, -94.64) * mm});
            skArc(sketch, "E354.MirrorCS", {"start": v(86.88, 45.33) * mm, "mid": v(94.66, 56.84) * mm, "end": v(92.74, 70.59) * mm});
            skArc(sketch, "E355.MirrorCS", {"start": v(283.9, -47.98) * mm, "mid": v(274.78, -42.6) * mm, "end": v(264.19, -42.87) * mm});
            skLineSegment(sketch, "E356.MirrorCS", {"start": v(203.86, -3) * mm, "end": v(177.11, -3) * mm});
            skLineSegment(sketch, "E357.MirrorCS", {"start": v(207.4, 94.64) * mm, "end": v(221.6, 94.64) * mm});
            skArc(sketch, "E358.MirrorCS", {"start": v(202.14, -45.33) * mm, "mid": v(209.92, -56.84) * mm, "end": v(208, -70.59) * mm});
            skLineSegment(sketch, "E359.MirrorCS", {"start": v(253.62, -94.64) * mm, "end": v(239.41, -94.64) * mm});
            skCircle(sketch, "E360.MirrorC", {"center": v(191.06, -61.2) * mm, "radius": 10.77 * mm});
            skLineSegment(sketch, "E361.MirrorCS", {"start": v(177.11, -47.98) * mm, "end": v(177.11, -3) * mm});
            skLineSegment(sketch, "E362.MirrorCS", {"start": v(196.83, -42.87) * mm, "end": v(196.83, -19.6) * mm});
            skLineSegment(sketch, "E363.MirrorCS", {"start": v(258.9, -100.89) * mm, "end": v(258.9, -75.88) * mm});
            skLineSegment(sketch, "E364.MirrorCS", {"start": v(143.64, 100.89) * mm, "end": v(143.64, 75.88) * mm});
            skLineSegment(sketch, "E365.MirrorCS", {"start": v(167.68, -75.12) * mm, "end": v(167.68, -100.89) * mm});
            skArc(sketch, "E366.MirrorCS", {"start": v(168.65, 47.98) * mm, "mid": v(159.52, 42.6) * mm, "end": v(148.93, 42.87) * mm});
            skArc(sketch, "E367.MirrorCS", {"start": v(143.63, 45.33) * mm, "mid": v(135.85, 56.84) * mm, "end": v(137.77, 70.59) * mm});
            skLineSegment(sketch, "E368.MirrorCS", {"start": v(141.9, 3) * mm, "end": v(168.65, 3) * mm});
            skLineSegment(sketch, "E369.MirrorCS", {"start": v(100.25, 70.59) * mm, "end": v(100.25, 36.2) * mm});
            skLineSegment(sketch, "E370.MirrorCS", {"start": v(83.5, 8.78) * mm, "end": v(67.67, 8.78) * mm});
            skCircle(sketch, "E371.MirrorC", {"center": v(75.8, -61.2) * mm, "radius": 10.77 * mm});
            skArc(sketch, "E372.MirrorCS", {"start": v(100.25, -36.2) * mm, "mid": v(93.09, -32.32) * mm, "end": v(86.88, -27.02) * mm});
            skArc(sketch, "E373.MirrorCS", {"start": v(61.86, -47.98) * mm, "mid": v(70.99, -42.6) * mm, "end": v(81.58, -42.87) * mm});
            skArc(sketch, "E374.MirrorCS", {"start": v(61.86, 47.98) * mm, "mid": v(70.99, 42.6) * mm, "end": v(81.58, 42.87) * mm});
            skLineSegment(sketch, "E375.MirrorCS", {"start": v(262.26, -8.78) * mm, "end": v(278.1, -8.78) * mm});
            skArc(sketch, "E376.MirrorCS", {"start": v(147, -8.78) * mm, "mid": v(138.51, -23.35) * mm, "end": v(123.92, -31.82) * mm});
            skLineSegment(sketch, "E377.MirrorCS", {"start": v(162.84, 37.04) * mm, "end": v(162.84, 8.78) * mm});
            skCircle(sketch, "E378.MirrorC", {"center": v(75.8, 61.2) * mm, "radius": 10.77 * mm});
            skLineSegment(sketch, "E379.MirrorCS", {"start": v(92.14, 94.64) * mm, "end": v(106.35, 94.64) * mm});
            skLineSegment(sketch, "E380.MirrorCS", {"start": v(81.1, -79.48) * mm, "end": v(81.1, -100.89) * mm});
            skLineSegment(sketch, "E381.MirrorCS", {"start": v(62.83, -75.12) * mm, "end": v(62.83, -100.89) * mm});
            skArc(sketch, "E382.MirrorCS", {"start": v(283.9, 47.98) * mm, "mid": v(274.78, 42.6) * mm, "end": v(264.19, 42.87) * mm});
            skLineSegment(sketch, "E383.MirrorCS", {"start": v(258.9, 100.89) * mm, "end": v(258.9, 75.88) * mm});
            skLineSegment(sketch, "E384.MirrorCS", {"start": v(278.1, -37.04) * mm, "end": v(278.1, -8.78) * mm});
            skLineSegment(sketch, "E385.MirrorCS", {"start": v(202.14, 27.02) * mm, "end": v(202.14, 45.33) * mm});
            skArc(sketch, "E386.MirrorCS", {"start": v(118.87, 26.62) * mm, "mid": v(134.45, 18.77) * mm, "end": v(141.9, 3) * mm});
            skLineSegment(sketch, "E387.MirrorCS", {"start": v(147, -8.78) * mm, "end": v(162.84, -8.78) * mm});
            skArc(sketch, "E388.MirrorCS", {"start": v(245.5, 36.2) * mm, "mid": v(252.68, 32.32) * mm, "end": v(258.88, 27.02) * mm});
            skLineSegment(sketch, "E389.MirrorCS", {"start": v(182.93, -37.04) * mm, "end": v(182.93, -8.78) * mm});
            skLineSegment(sketch, "E390.MirrorCS", {"start": v(207.4, 81.85) * mm, "end": v(207.4, 94.64) * mm});
            skArc(sketch, "E391.MirrorCS", {"start": v(198.76, 8.78) * mm, "mid": v(207.25, 23.35) * mm, "end": v(221.84, 31.82) * mm});
            skArc(sketch, "E392.MirrorCS", {"start": v(81.1, 79.48) * mm, "mid": v(71.39, 79.71) * mm, "end": v(62.83, 75.12) * mm});
            skArc(sketch, "E393.MirrorCS", {"start": v(111.64, 26.62) * mm, "mid": v(96.06, 18.77) * mm, "end": v(88.6, 3) * mm});
            skLineSegment(sketch, "E394.MirrorCS", {"start": v(75.09, 19.6) * mm, "end": v(75.09, 35.72) * mm});
            skLineSegment(sketch, "E395.MirrorCS", {"start": v(282.94, 100.89) * mm, "end": v(264.66, 100.89) * mm});
            skLineSegment(sketch, "E396.MirrorCS", {"start": v(226.9, 26.62) * mm, "end": v(226.9, 100.89) * mm});
            skArc(sketch, "E397.MirrorCS", {"start": v(215.5, -36.2) * mm, "mid": v(208.34, -32.32) * mm, "end": v(202.14, -27.02) * mm});
            skLineSegment(sketch, "E398.MirrorCS", {"start": v(264.19, -42.87) * mm, "end": v(264.19, -19.6) * mm});
            skLineSegment(sketch, "E399.MirrorCS", {"start": v(283.9, 47.98) * mm, "end": v(283.9, 3) * mm});
            skLineSegment(sketch, "E400.MirrorCS", {"start": v(168.65, 47.98) * mm, "end": v(168.65, 3) * mm});
            skLineSegment(sketch, "E401.MirrorCS", {"start": v(124.16, 94.64) * mm, "end": v(123.92, 31.81) * mm});
            skArc(sketch, "E402.MirrorCS", {"start": v(149.4, -79.48) * mm, "mid": v(159.12, -79.71) * mm, "end": v(167.68, -75.12) * mm});
            skArc(sketch, "E403.MirrorCS", {"start": v(143.63, -45.33) * mm, "mid": v(135.85, -56.84) * mm, "end": v(137.77, -70.59) * mm});
            skArc(sketch, "E404.MirrorCS", {"start": v(130.26, -36.2) * mm, "mid": v(137.42, -32.32) * mm, "end": v(143.63, -27.02) * mm});
            skLineSegment(sketch, "E405.MirrorCS", {"start": v(143.63, 27.02) * mm, "end": v(143.63, 45.33) * mm});
            skLineSegment(sketch, "E406.MirrorCS", {"start": v(282.94, 75.12) * mm, "end": v(282.94, 100.89) * mm});
            skLineSegment(sketch, "E407.MirrorCS", {"start": v(81.58, -42.87) * mm, "end": v(81.58, -19.6) * mm});
            skLineSegment(sketch, "E408.MirrorCS", {"start": v(86.87, 100.89) * mm, "end": v(111.64, 100.89) * mm});
            skLineSegment(sketch, "E409.MirrorCS", {"start": v(100.25, -70.59) * mm, "end": v(100.25, -36.2) * mm});
            skLineSegment(sketch, "E410.MirrorCS", {"start": v(92.14, -94.64) * mm, "end": v(106.35, -94.64) * mm});
            skLineSegment(sketch, "E411.MirrorCS", {"start": v(178.08, 75.12) * mm, "end": v(178.08, 100.89) * mm});
            skLineSegment(sketch, "E412.MirrorCS", {"start": v(253.62, 81.85) * mm, "end": v(253.62, 94.64) * mm});
            skLineSegment(sketch, "E413.MirrorCS", {"start": v(264.19, 42.87) * mm, "end": v(264.19, 19.6) * mm});
            skLineSegment(sketch, "E414.MirrorCS", {"start": v(215.5, -70.59) * mm, "end": v(215.5, -36.2) * mm});
            skArc(sketch, "E415.MirrorCS", {"start": v(258.88, 45.33) * mm, "mid": v(251.1, 56.84) * mm, "end": v(253.03, 70.59) * mm});
            skArc(sketch, "E416.MirrorCS", {"start": v(264.66, -79.48) * mm, "mid": v(274.38, -79.71) * mm, "end": v(282.94, -75.12) * mm});
            skArc(sketch, "E417.MirrorCS", {"start": v(262.26, -8.78) * mm, "mid": v(253.77, -23.35) * mm, "end": v(239.18, -31.82) * mm});
            skLineSegment(sketch, "E418.MirrorCS", {"start": v(239.41, -94.64) * mm, "end": v(239.18, -31.81) * mm});
            skLineSegment(sketch, "E419.MirrorCS", {"start": v(198.76, -8.78) * mm, "end": v(182.93, -8.78) * mm});
            skArc(sketch, "E420.MirrorCS", {"start": v(118.87, -26.62) * mm, "mid": v(134.45, -18.77) * mm, "end": v(141.9, -3) * mm});
            skLineSegment(sketch, "E421.MirrorCS", {"start": v(149.4, -79.48) * mm, "end": v(149.4, -100.89) * mm});
            skArc(sketch, "E422.MirrorCS", {"start": v(130.26, 36.2) * mm, "mid": v(137.42, 32.32) * mm, "end": v(143.63, 27.02) * mm});
            skLineSegment(sketch, "E423.MirrorCS", {"start": v(138.37, -81.85) * mm, "end": v(138.37, -94.64) * mm});
            skArc(sketch, "E424.MirrorCS", {"start": v(168.65, -47.98) * mm, "mid": v(159.52, -42.6) * mm, "end": v(148.93, -42.87) * mm});
            skLineSegment(sketch, "E425.MirrorCS", {"start": v(62.83, 75.12) * mm, "end": v(62.83, 100.89) * mm});
            skLineSegment(sketch, "E426.MirrorCS", {"start": v(61.86, 47.98) * mm, "end": v(61.86, 3) * mm});
            skLineSegment(sketch, "E427.MirrorCS", {"start": v(221.6, -94.64) * mm, "end": v(221.84, -31.81) * mm});
            skCircle(sketch, "E428.MirrorC", {"center": v(269.96, 61.2) * mm, "radius": 10.77 * mm});
            skCircle(sketch, "E429.MirrorC", {"center": v(191.06, 61.2) * mm, "radius": 10.77 * mm});
            skLineSegment(sketch, "E430.MirrorCS", {"start": v(258.88, -27.02) * mm, "end": v(258.88, -45.33) * mm});
            skLineSegment(sketch, "E431.MirrorCS", {"start": v(258.9, 100.89) * mm, "end": v(234.12, 100.89) * mm});
            skLineSegment(sketch, "E432.MirrorCS", {"start": v(283.9, -47.98) * mm, "end": v(283.9, -3) * mm});
            skLineSegment(sketch, "E433.MirrorCS", {"start": v(203.86, 3) * mm, "end": v(177.11, 3) * mm});
            skArc(sketch, "E434.MirrorCS", {"start": v(202.14, 45.33) * mm, "mid": v(209.92, 56.84) * mm, "end": v(208, 70.59) * mm});
            skArc(sketch, "E435.MirrorCS", {"start": v(234.12, -26.62) * mm, "mid": v(249.7, -18.77) * mm, "end": v(257.16, -3) * mm});
            skLineSegment(sketch, "E436.MirrorCS", {"start": v(178.08, 100.89) * mm, "end": v(196.35, 100.89) * mm});
            skLineSegment(sketch, "E437.MirrorCS", {"start": v(143.63, -27.02) * mm, "end": v(143.63, -45.33) * mm});
            skLineSegment(sketch, "E438.MirrorCS", {"start": v(155.42, 19.6) * mm, "end": v(155.42, 35.72) * mm});
            skCircle(sketch, "E439.MirrorC", {"center": v(154.7, -61.2) * mm, "radius": 10.77 * mm});
            skLineSegment(sketch, "E440.MirrorCS", {"start": v(118.87, 26.62) * mm, "end": v(118.87, 100.89) * mm});
            skLineSegment(sketch, "E441.MirrorCS", {"start": v(130.26, -70.59) * mm, "end": v(130.26, -36.2) * mm});
            skLineSegment(sketch, "E442.MirrorCS", {"start": v(86.88, -27.02) * mm, "end": v(86.88, -45.33) * mm});
            skLineSegment(sketch, "E443.MirrorCS", {"start": v(111.64, 26.62) * mm, "end": v(111.64, 100.89) * mm});
            skLineSegment(sketch, "E444.MirrorCS", {"start": v(61.86, -47.98) * mm, "end": v(61.86, -3) * mm});
            skLineSegment(sketch, "E445.MirrorCS", {"start": v(253.62, 94.64) * mm, "end": v(239.41, 94.64) * mm});
            skLineSegment(sketch, "E446.MirrorCS", {"start": v(245.5, -70.59) * mm, "end": v(245.5, -36.2) * mm});
            skLineSegment(sketch, "E447.MirrorCS", {"start": v(234.12, 26.62) * mm, "end": v(234.12, 100.89) * mm});
            skLineSegment(sketch, "E448.MirrorCS", {"start": v(196.35, -79.48) * mm, "end": v(196.35, -100.89) * mm});
            skArc(sketch, "E449.MirrorCS", {"start": v(177.11, -47.98) * mm, "mid": v(186.24, -42.6) * mm, "end": v(196.83, -42.87) * mm});
            skArc(sketch, "E450.MirrorCS", {"start": v(177.11, 47.98) * mm, "mid": v(186.24, 42.6) * mm, "end": v(196.83, 42.87) * mm});
            skArc(sketch, "E451.MirrorCS", {"start": v(264.66, 79.48) * mm, "mid": v(274.38, 79.71) * mm, "end": v(282.94, 75.12) * mm});
            skLineSegment(sketch, "E452.MirrorCS", {"start": v(149.4, 79.48) * mm, "end": v(149.4, 100.89) * mm});
            skLineSegment(sketch, "E453.MirrorCS", {"start": v(118.87, -26.62) * mm, "end": v(118.87, -100.89) * mm});
            skLineSegment(sketch, "E454.MirrorCS", {"start": v(147, 8.78) * mm, "end": v(162.84, 8.78) * mm});
            skArc(sketch, "E455.MirrorCS", {"start": v(86.88, -45.33) * mm, "mid": v(94.66, -56.84) * mm, "end": v(92.74, -70.59) * mm});
            skArc(sketch, "E456.MirrorCS", {"start": v(81.1, -79.48) * mm, "mid": v(71.39, -79.71) * mm, "end": v(62.83, -75.12) * mm});
            skLineSegment(sketch, "E457.MirrorCS", {"start": v(106.35, 94.64) * mm, "end": v(106.59, 31.81) * mm});
            skLineSegment(sketch, "E458.MirrorCS", {"start": v(264.66, -79.48) * mm, "end": v(264.66, -100.89) * mm});
            skLineSegment(sketch, "E459.MirrorCS", {"start": v(270.68, -19.6) * mm, "end": v(270.68, -35.72) * mm});
            skLineSegment(sketch, "E460.MirrorCS", {"start": v(202.13, 100.89) * mm, "end": v(202.13, 75.88) * mm});
            skArc(sketch, "E461.MirrorCS", {"start": v(226.9, 26.62) * mm, "mid": v(211.32, 18.77) * mm, "end": v(203.86, 3) * mm});
            skLineSegment(sketch, "E462.MirrorCS", {"start": v(177.11, 47.98) * mm, "end": v(177.11, 3) * mm});
            skLineSegment(sketch, "E463.MirrorCS", {"start": v(138.37, 81.85) * mm, "end": v(138.37, 94.64) * mm});
            skLineSegment(sketch, "E464.MirrorCS", {"start": v(148.93, 42.87) * mm, "end": v(148.93, 19.6) * mm});
            skLineSegment(sketch, "E465.MirrorCS", {"start": v(155.42, -19.6) * mm, "end": v(155.42, -35.72) * mm});
            skLineSegment(sketch, "E466.MirrorCS", {"start": v(138.37, 94.64) * mm, "end": v(124.16, 94.64) * mm});
            skLineSegment(sketch, "E467.MirrorCS", {"start": v(282.94, -75.12) * mm, "end": v(282.94, -100.89) * mm});
            skLineSegment(sketch, "E468.MirrorCS", {"start": v(257.16, -3) * mm, "end": v(283.9, -3) * mm});
            skArc(sketch, "E469.MirrorCS", {"start": v(226.9, -26.62) * mm, "mid": v(211.32, -18.77) * mm, "end": v(203.86, -3) * mm});
            skLineSegment(sketch, "E470.MirrorCS", {"start": v(138.37, -94.64) * mm, "end": v(124.16, -94.64) * mm});
            skLineSegment(sketch, "E471.MirrorCS", {"start": v(67.67, 37.04) * mm, "end": v(67.67, 8.78) * mm});
            skLineSegment(sketch, "E472.MirrorCS", {"start": v(75.09, -19.6) * mm, "end": v(75.09, -35.72) * mm});
            skLineSegment(sketch, "E473.MirrorCS", {"start": v(88.6, -3) * mm, "end": v(61.86, -3) * mm});
            skLineSegment(sketch, "E474.MirrorCS", {"start": v(257.16, 3) * mm, "end": v(283.9, 3) * mm});
            skArc(sketch, "E475.MirrorCS", {"start": v(147, 8.78) * mm, "mid": v(138.51, 23.35) * mm, "end": v(123.92, 31.82) * mm});
            skArc(sketch, "E476.MirrorCS", {"start": v(262.26, 8.78) * mm, "mid": v(253.77, 23.35) * mm, "end": v(239.18, 31.82) * mm});
            skLineSegment(sketch, "E477.MirrorCS", {"start": v(62.83, 100.89) * mm, "end": v(81.1, 100.89) * mm});
            skLineSegment(sketch, "E478.MirrorCS", {"start": v(67.67, -37.04) * mm, "end": v(67.67, -8.78) * mm});
            skLineSegment(sketch, "E479.MirrorCS", {"start": v(258.9, -100.89) * mm, "end": v(234.12, -100.89) * mm});
            skLineSegment(sketch, "E480.MirrorCS", {"start": v(270.68, 19.6) * mm, "end": v(270.68, 35.72) * mm});
            skLineSegment(sketch, "E481.MirrorCS", {"start": v(258.88, 27.02) * mm, "end": v(258.88, 45.33) * mm});
            skLineSegment(sketch, "E482.MirrorCS", {"start": v(168.65, -47.98) * mm, "end": v(168.65, -3) * mm});
            skArc(sketch, "E483.MirrorCS", {"start": v(83.5, 8.78) * mm, "mid": v(92, 23.35) * mm, "end": v(106.59, 31.82) * mm});
            skLineSegment(sketch, "E484.MirrorCS", {"start": v(86.87, -100.89) * mm, "end": v(86.87, -75.88) * mm});
            skLineSegment(sketch, "E485.MirrorCS", {"start": v(86.88, 27.02) * mm, "end": v(86.88, 45.33) * mm});
            skLineSegment(sketch, "E486.MirrorCS", {"start": v(198.76, 8.78) * mm, "end": v(182.93, 8.78) * mm});
            skLineSegment(sketch, "E487.MirrorCS", {"start": v(178.08, -75.12) * mm, "end": v(178.08, -100.89) * mm});
            skLineSegment(sketch, "E488.MirrorCS", {"start": v(167.68, 100.89) * mm, "end": v(149.4, 100.89) * mm});
            skLineSegment(sketch, "E489.MirrorCS", {"start": v(130.26, 70.59) * mm, "end": v(130.26, 36.2) * mm});
            skLineSegment(sketch, "E490.MirrorCS", {"start": v(143.64, -100.89) * mm, "end": v(143.64, -75.88) * mm});
            skLineSegment(sketch, "E491.MirrorCS", {"start": v(81.1, 79.48) * mm, "end": v(81.1, 100.89) * mm});
            skLineSegment(sketch, "E492.MirrorCS", {"start": v(226.9, -26.62) * mm, "end": v(226.9, -100.89) * mm});
            skLineSegment(sketch, "E493.MirrorCS", {"start": v(245.5, 70.59) * mm, "end": v(245.5, 36.2) * mm});
            skLineSegment(sketch, "E494.MirrorCS", {"start": v(215.5, 70.59) * mm, "end": v(215.5, 36.2) * mm});
            skLineSegment(sketch, "E495.MirrorCS", {"start": v(141.9, -3) * mm, "end": v(168.65, -3) * mm});
            skLineSegment(sketch, "E496.MirrorCS", {"start": v(81.58, 42.87) * mm, "end": v(81.58, 19.6) * mm});
            skLineSegment(sketch, "E497.MirrorCS", {"start": v(234.12, -26.62) * mm, "end": v(234.12, -100.89) * mm});
            skArc(sketch, "E498.MirrorCS", {"start": v(258.88, -45.33) * mm, "mid": v(251.1, -56.84) * mm, "end": v(253.03, -70.59) * mm});
            skLineSegment(sketch, "E499.MirrorCS", {"start": v(207.4, -81.85) * mm, "end": v(207.4, -94.64) * mm});
            skArc(sketch, "E500.MirrorCS", {"start": v(196.35, 79.48) * mm, "mid": v(186.64, 79.71) * mm, "end": v(178.08, 75.12) * mm});
            skLineSegment(sketch, "E501.MirrorCS", {"start": v(262.26, 8.78) * mm, "end": v(278.1, 8.78) * mm});
            skCircle(sketch, "E502.MirrorC", {"center": v(154.7, 61.2) * mm, "radius": 10.77 * mm});
            skLineSegment(sketch, "E503.MirrorCS", {"start": v(239.41, 94.64) * mm, "end": v(239.18, 31.81) * mm});
            skArc(sketch, "E504.MirrorCS", {"start": v(111.64, -26.62) * mm, "mid": v(96.06, -18.77) * mm, "end": v(88.6, -3) * mm});
            skCircle(sketch, "E505.MirrorC", {"center": v(115.25, 0) * mm, "radius": 20.2 * mm});
            skCircle(sketch, "E506.MirrorC", {"center": v(230.5, 0) * mm, "radius": 20.2 * mm});
            skLineSegment(sketch, "E507.MirrorCS", {"start": v(-288.14, -105.78) * mm, "end": v(-288.14, 105.78) * mm});
            skLineSegment(sketch, "E508.MirrorCS", {"start": v(-288.14, 105.78) * mm, "end": v(-288.14, -105.78) * mm});
            skLineSegment(sketch, "E509.MirrorCS", {"start": v(-288.14, -105.78) * mm, "end": v(-403.4, -105.78) * mm});
            skLineSegment(sketch, "E510.MirrorCS", {"start": v(-288.14, 105.78) * mm, "end": v(-403.4, 105.78) * mm});
            skLineSegment(sketch, "E511.MirrorCS", {"start": v(-172.88, 105.78) * mm, "end": v(-288.14, 105.78) * mm});
            skLineSegment(sketch, "E512.MirrorCS", {"start": v(-403.4, -105.78) * mm, "end": v(-403.4, 105.78) * mm});
            skLineSegment(sketch, "E513.MirrorCS", {"start": v(-172.88, -105.78) * mm, "end": v(-288.14, -105.78) * mm});
            skLineSegment(sketch, "E514.MirrorCS", {"start": v(-403.4, 105.78) * mm, "end": v(-288.14, 105.78) * mm});
            skLineSegment(sketch, "E515.MirrorCS", {"start": v(-288.14, 105.78) * mm, "end": v(-172.88, 105.78) * mm});
            skLineSegment(sketch, "E516.MirrorCS", {"start": v(-288.14, -105.78) * mm, "end": v(-172.88, -105.78) * mm});
            skLineSegment(sketch, "E517.MirrorCS", {"start": v(-403.4, -105.78) * mm, "end": v(-288.14, -105.78) * mm});
            skLineSegment(sketch, "E518.MirrorCS", {"start": v(-403.4, 105.78) * mm, "end": v(-403.4, -105.78) * mm});
            skLineSegment(sketch, "E519.MirrorCS", {"start": v(-360.76, 75.88) * mm, "end": v(-360.76, 81.85) * mm});
            skLineSegment(sketch, "E520.MirrorCS", {"start": v(-330.76, -75.88) * mm, "end": v(-317.38, -75.88) * mm});
            skLineSegment(sketch, "E521.MirrorCS", {"start": v(-385.93, -19.6) * mm, "end": v(-379.44, -19.6) * mm});
            skLineSegment(sketch, "E522.MirrorCS", {"start": v(-215.5, 75.88) * mm, "end": v(-215.5, 81.85) * mm});
            skArc(sketch, "E523.MirrorCS", {"start": v(-305.6, 35.72) * mm, "mid": v(-301.84, 36.1) * mm, "end": v(-298.18, 37.04) * mm});
            skLineSegment(sketch, "E524.MirrorCS", {"start": v(-305.6, 19.6) * mm, "end": v(-312.09, 19.6) * mm});
            skLineSegment(sketch, "E525.MirrorCS", {"start": v(-368.86, 70.59) * mm, "end": v(-360.76, 70.59) * mm});
            skLineSegment(sketch, "E526.MirrorCS", {"start": v(-385.93, 19.6) * mm, "end": v(-379.44, 19.6) * mm});
            skLineSegment(sketch, "E527.MirrorCS", {"start": v(-245.5, -75.88) * mm, "end": v(-258.9, -75.88) * mm});
            skArc(sketch, "E528.MirrorCS", {"start": v(-305.6, -35.72) * mm, "mid": v(-301.84, -36.1) * mm, "end": v(-298.18, -37.04) * mm});
            skLineSegment(sketch, "E529.MirrorCS", {"start": v(-360.76, 75.88) * mm, "end": v(-374.15, 75.88) * mm});
            skLineSegment(sketch, "E530.MirrorCS", {"start": v(-245.5, 75.88) * mm, "end": v(-258.9, 75.88) * mm});
            skLineSegment(sketch, "E531.MirrorCS", {"start": v(-207.42, -70.59) * mm, "end": v(-215.5, -70.59) * mm});
            skArc(sketch, "E532.MirrorCS", {"start": v(-385.93, 35.72) * mm, "mid": v(-389.69, 36.1) * mm, "end": v(-393.35, 37.04) * mm});
            skLineSegment(sketch, "E533.MirrorCS", {"start": v(-207.4, 81.85) * mm, "end": v(-215.5, 81.85) * mm});
            skLineSegment(sketch, "E534.MirrorCS", {"start": v(-330.76, 75.88) * mm, "end": v(-317.38, 75.88) * mm});
            skLineSegment(sketch, "E535.MirrorCS", {"start": v(-317.38, -100.89) * mm, "end": v(-317.38, -75.88) * mm});
            skLineSegment(sketch, "E536.MirrorCS", {"start": v(-270.68, -19.6) * mm, "end": v(-264.19, -19.6) * mm});
            skLineSegment(sketch, "E537.MirrorCS", {"start": v(-190.34, -19.6) * mm, "end": v(-196.83, -19.6) * mm});
            skLineSegment(sketch, "E538.MirrorCS", {"start": v(-215.5, -75.88) * mm, "end": v(-215.5, -81.85) * mm});
            skLineSegment(sketch, "E539.MirrorCS", {"start": v(-253.62, 81.85) * mm, "end": v(-245.5, 81.85) * mm});
            skLineSegment(sketch, "E540.MirrorCS", {"start": v(-245.5, -75.88) * mm, "end": v(-245.5, -81.85) * mm});
            skLineSegment(sketch, "E541.MirrorCS", {"start": v(-330.76, 75.88) * mm, "end": v(-330.76, 81.85) * mm});
            skLineSegment(sketch, "E542.MirrorCS", {"start": v(-360.76, -75.88) * mm, "end": v(-360.76, -81.85) * mm});
            skLineSegment(sketch, "E543.MirrorCS", {"start": v(-190.34, 19.6) * mm, "end": v(-196.83, 19.6) * mm});
            skLineSegment(sketch, "E544.MirrorCS", {"start": v(-322.67, 70.59) * mm, "end": v(-330.76, 70.59) * mm});
            skLineSegment(sketch, "E545.MirrorCS", {"start": v(-270.68, 19.6) * mm, "end": v(-264.19, 19.6) * mm});
            skArc(sketch, "E546.MirrorCS", {"start": v(-190.34, 35.72) * mm, "mid": v(-186.59, 36.1) * mm, "end": v(-182.93, 37.04) * mm});
            skLineSegment(sketch, "E547.MirrorCS", {"start": v(-322.65, 81.85) * mm, "end": v(-330.76, 81.85) * mm});
            skArc(sketch, "E548.MirrorCS", {"start": v(-270.68, -35.72) * mm, "mid": v(-274.43, -36.1) * mm, "end": v(-278.1, -37.04) * mm});
            skLineSegment(sketch, "E549.MirrorCS", {"start": v(-368.87, -81.85) * mm, "end": v(-360.76, -81.85) * mm});
            skLineSegment(sketch, "E550.MirrorCS", {"start": v(-245.5, 75.88) * mm, "end": v(-245.5, 81.85) * mm});
            skLineSegment(sketch, "E551.MirrorCS", {"start": v(-330.76, -75.88) * mm, "end": v(-330.76, -81.85) * mm});
            skLineSegment(sketch, "E552.MirrorCS", {"start": v(-207.4, -81.85) * mm, "end": v(-207.4, -94.64) * mm});
            skLineSegment(sketch, "E553.MirrorCS", {"start": v(-368.86, -70.59) * mm, "end": v(-360.76, -70.59) * mm});
            skArc(sketch, "E554.MirrorCS", {"start": v(-270.68, 35.72) * mm, "mid": v(-274.43, 36.1) * mm, "end": v(-278.1, 37.04) * mm});
            skArc(sketch, "E555.MirrorCS", {"start": v(-385.93, -35.72) * mm, "mid": v(-389.69, -36.1) * mm, "end": v(-393.35, -37.04) * mm});
            skLineSegment(sketch, "E556.MirrorCS", {"start": v(-360.76, -75.88) * mm, "end": v(-374.15, -75.88) * mm});
            skLineSegment(sketch, "E557.MirrorCS", {"start": v(-368.87, -81.85) * mm, "end": v(-368.87, -94.64) * mm});
            skLineSegment(sketch, "E558.MirrorCS", {"start": v(-368.87, 94.64) * mm, "end": v(-354.67, 94.64) * mm});
            skLineSegment(sketch, "E559.MirrorCS", {"start": v(-202.13, 100.89) * mm, "end": v(-202.13, 75.88) * mm});
            skLineSegment(sketch, "E560.MirrorCS", {"start": v(-322.65, -81.85) * mm, "end": v(-322.65, -94.64) * mm});
            skLineSegment(sketch, "E561.MirrorCS", {"start": v(-368.87, -94.64) * mm, "end": v(-354.67, -94.64) * mm});
            skLineSegment(sketch, "E562.MirrorCS", {"start": v(-368.87, 81.85) * mm, "end": v(-360.76, 81.85) * mm});
            skLineSegment(sketch, "E563.MirrorCS", {"start": v(-322.65, 81.85) * mm, "end": v(-322.65, 94.64) * mm});
            skLineSegment(sketch, "E564.MirrorCS", {"start": v(-368.87, 81.85) * mm, "end": v(-368.87, 94.64) * mm});
            skLineSegment(sketch, "E565.MirrorCS", {"start": v(-305.6, -19.6) * mm, "end": v(-312.09, -19.6) * mm});
            skLineSegment(sketch, "E566.MirrorCS", {"start": v(-253.6, 70.59) * mm, "end": v(-245.5, 70.59) * mm});
            skLineSegment(sketch, "E567.MirrorCS", {"start": v(-253.62, -81.85) * mm, "end": v(-253.62, -94.64) * mm});
            skLineSegment(sketch, "E568.MirrorCS", {"start": v(-207.42, 70.59) * mm, "end": v(-215.5, 70.59) * mm});
            skLineSegment(sketch, "E569.MirrorCS", {"start": v(-253.6, -70.59) * mm, "end": v(-245.5, -70.59) * mm});
            skLineSegment(sketch, "E570.MirrorCS", {"start": v(-317.38, 100.89) * mm, "end": v(-317.38, 75.88) * mm});
            skLineSegment(sketch, "E571.MirrorCS", {"start": v(-207.4, 81.85) * mm, "end": v(-207.4, 94.64) * mm});
            skLineSegment(sketch, "E572.MirrorCS", {"start": v(-202.13, -100.89) * mm, "end": v(-202.13, -75.88) * mm});
            skLineSegment(sketch, "E573.MirrorCS", {"start": v(-207.4, -81.85) * mm, "end": v(-215.5, -81.85) * mm});
            skLineSegment(sketch, "E574.MirrorCS", {"start": v(-253.62, -81.85) * mm, "end": v(-245.5, -81.85) * mm});
            skLineSegment(sketch, "E575.MirrorCS", {"start": v(-215.5, 75.88) * mm, "end": v(-202.13, 75.88) * mm});
            skArc(sketch, "E576.MirrorCS", {"start": v(-190.34, -35.72) * mm, "mid": v(-186.59, -36.1) * mm, "end": v(-182.93, -37.04) * mm});
            skLineSegment(sketch, "E577.MirrorCS", {"start": v(-215.5, -75.88) * mm, "end": v(-202.13, -75.88) * mm});
            skLineSegment(sketch, "E578.MirrorCS", {"start": v(-253.62, 81.85) * mm, "end": v(-253.62, 94.64) * mm});
            skLineSegment(sketch, "E579.MirrorCS", {"start": v(-322.67, -70.59) * mm, "end": v(-330.76, -70.59) * mm});
            skLineSegment(sketch, "E580.MirrorCS", {"start": v(-322.65, -81.85) * mm, "end": v(-330.76, -81.85) * mm});
            skLineSegment(sketch, "E581.MirrorCS", {"start": v(-398.2, 100.89) * mm, "end": v(-379.92, 100.89) * mm});
            skArc(sketch, "E582.MirrorCS", {"start": v(-379.92, 79.48) * mm, "mid": v(-389.63, 79.71) * mm, "end": v(-398.2, 75.12) * mm});
            skLineSegment(sketch, "E583.MirrorCS", {"start": v(-379.92, 79.48) * mm, "end": v(-379.92, 100.89) * mm});
            skLineSegment(sketch, "E584.MirrorCS", {"start": v(-374.15, 100.89) * mm, "end": v(-374.15, 75.88) * mm});
            skLineSegment(sketch, "E585.MirrorCS", {"start": v(-177.11, -47.98) * mm, "end": v(-177.11, -3) * mm});
            skLineSegment(sketch, "E586.MirrorCS", {"start": v(-317.38, 100.89) * mm, "end": v(-342.15, 100.89) * mm});
            skLineSegment(sketch, "E587.MirrorCS", {"start": v(-374.15, -100.89) * mm, "end": v(-374.15, -75.88) * mm});
            skLineSegment(sketch, "E588.MirrorCS", {"start": v(-202.13, 100.89) * mm, "end": v(-226.9, 100.89) * mm});
            skLineSegment(sketch, "E589.MirrorCS", {"start": v(-312.09, 42.87) * mm, "end": v(-312.09, 19.6) * mm});
            skArc(sketch, "E590.MirrorCS", {"start": v(-330.76, -36.2) * mm, "mid": v(-323.6, -32.32) * mm, "end": v(-317.4, -27.02) * mm});
            skLineSegment(sketch, "E591.MirrorCS", {"start": v(-190.34, 19.6) * mm, "end": v(-190.34, 35.72) * mm});
            skLineSegment(sketch, "E592.MirrorCS", {"start": v(-202.14, -27.02) * mm, "end": v(-202.14, -45.33) * mm});
            skLineSegment(sketch, "E593.MirrorCS", {"start": v(-292.37, -47.98) * mm, "end": v(-292.37, -3) * mm});
            skLineSegment(sketch, "E594.MirrorCS", {"start": v(-282.94, -100.89) * mm, "end": v(-264.66, -100.89) * mm});
            skLineSegment(sketch, "E595.MirrorCS", {"start": v(-245.5, -70.59) * mm, "end": v(-245.5, -36.2) * mm});
            skCircle(sketch, "E596.MirrorC", {"center": v(-385.2, 61.2) * mm, "radius": 10.77 * mm});
            skArc(sketch, "E597.MirrorCS", {"start": v(-196.35, -79.48) * mm, "mid": v(-186.64, -79.71) * mm, "end": v(-178.08, -75.12) * mm});
            skLineSegment(sketch, "E598.MirrorCS", {"start": v(-198.76, -8.78) * mm, "end": v(-182.93, -8.78) * mm});
            skLineSegment(sketch, "E599.MirrorCS", {"start": v(-379.92, -79.48) * mm, "end": v(-379.92, -100.89) * mm});
            skArc(sketch, "E600.MirrorCS", {"start": v(-283.9, -47.98) * mm, "mid": v(-274.78, -42.6) * mm, "end": v(-264.19, -42.87) * mm});
            skArc(sketch, "E601.MirrorCS", {"start": v(-264.66, 79.48) * mm, "mid": v(-274.38, 79.71) * mm, "end": v(-282.94, 75.12) * mm});
            skLineSegment(sketch, "E602.MirrorCS", {"start": v(-379.44, 42.87) * mm, "end": v(-379.44, 19.6) * mm});
            skLineSegment(sketch, "E603.MirrorCS", {"start": v(-178.08, 75.12) * mm, "end": v(-178.08, 100.89) * mm});
            skLineSegment(sketch, "E604.MirrorCS", {"start": v(-190.34, -19.6) * mm, "end": v(-190.34, -35.72) * mm});
            skArc(sketch, "E605.MirrorCS", {"start": v(-262.26, -8.78) * mm, "mid": v(-253.77, -23.35) * mm, "end": v(-239.18, -31.82) * mm});
            skArc(sketch, "E606.MirrorCS", {"start": v(-314.01, 8.78) * mm, "mid": v(-322.5, 23.35) * mm, "end": v(-337.1, 31.82) * mm});
            skLineSegment(sketch, "E607.MirrorCS", {"start": v(-349.38, -26.62) * mm, "end": v(-349.38, -100.89) * mm});
            skLineSegment(sketch, "E608.MirrorCS", {"start": v(-203.86, 3) * mm, "end": v(-177.11, 3) * mm});
            skArc(sketch, "E609.MirrorCS", {"start": v(-342.15, -26.62) * mm, "mid": v(-326.57, -18.77) * mm, "end": v(-319.11, -3) * mm});
            skLineSegment(sketch, "E610.MirrorCS", {"start": v(-234.12, -26.62) * mm, "end": v(-234.12, -100.89) * mm});
            skArc(sketch, "E611.MirrorCS", {"start": v(-177.11, -47.98) * mm, "mid": v(-186.24, -42.6) * mm, "end": v(-196.83, -42.87) * mm});
            skLineSegment(sketch, "E612.MirrorCS", {"start": v(-258.88, 27.02) * mm, "end": v(-258.88, 45.33) * mm});
            skLineSegment(sketch, "E613.MirrorCS", {"start": v(-264.66, -79.48) * mm, "end": v(-264.66, -100.89) * mm});
            skLineSegment(sketch, "E614.MirrorCS", {"start": v(-322.65, 94.64) * mm, "end": v(-336.86, 94.64) * mm});
            skLineSegment(sketch, "E615.MirrorCS", {"start": v(-377.51, 8.78) * mm, "end": v(-393.35, 8.78) * mm});
            skLineSegment(sketch, "E616.MirrorCS", {"start": v(-215.5, 70.59) * mm, "end": v(-215.5, 36.2) * mm});
            skLineSegment(sketch, "E617.MirrorCS", {"start": v(-293.33, 100.89) * mm, "end": v(-311.6, 100.89) * mm});
            skArc(sketch, "E618.MirrorCS", {"start": v(-215.5, -36.2) * mm, "mid": v(-208.34, -32.32) * mm, "end": v(-202.14, -27.02) * mm});
            skLineSegment(sketch, "E619.MirrorCS", {"start": v(-305.6, 19.6) * mm, "end": v(-305.6, 35.72) * mm});
            skLineSegment(sketch, "E620.MirrorCS", {"start": v(-319.11, -3) * mm, "end": v(-292.37, -3) * mm});
            skArc(sketch, "E621.MirrorCS", {"start": v(-311.6, 79.48) * mm, "mid": v(-301.9, 79.71) * mm, "end": v(-293.33, 75.12) * mm});
            skLineSegment(sketch, "E622.MirrorCS", {"start": v(-374.15, -100.89) * mm, "end": v(-349.38, -100.89) * mm});
            skLineSegment(sketch, "E623.MirrorCS", {"start": v(-245.5, 70.59) * mm, "end": v(-245.5, 36.2) * mm});
            skArc(sketch, "E624.MirrorCS", {"start": v(-196.35, 79.48) * mm, "mid": v(-186.64, 79.71) * mm, "end": v(-178.08, 75.12) * mm});
            skLineSegment(sketch, "E625.MirrorCS", {"start": v(-360.76, 70.59) * mm, "end": v(-360.76, 36.2) * mm});
            skLineSegment(sketch, "E626.MirrorCS", {"start": v(-258.88, -27.02) * mm, "end": v(-258.88, -45.33) * mm});
            skLineSegment(sketch, "E627.MirrorCS", {"start": v(-336.86, 94.64) * mm, "end": v(-337.1, 31.81) * mm});
            skLineSegment(sketch, "E628.MirrorCS", {"start": v(-270.68, 19.6) * mm, "end": v(-270.68, 35.72) * mm});
            skLineSegment(sketch, "E629.MirrorCS", {"start": v(-202.14, 27.02) * mm, "end": v(-202.14, 45.33) * mm});
            skArc(sketch, "E630.MirrorCS", {"start": v(-177.11, 47.98) * mm, "mid": v(-186.24, 42.6) * mm, "end": v(-196.83, 42.87) * mm});
            skArc(sketch, "E631.MirrorCS", {"start": v(-374.14, 45.33) * mm, "mid": v(-366.36, 56.84) * mm, "end": v(-368.28, 70.59) * mm});
            skLineSegment(sketch, "E632.MirrorCS", {"start": v(-178.08, -100.89) * mm, "end": v(-196.35, -100.89) * mm});
            skLineSegment(sketch, "E633.MirrorCS", {"start": v(-207.4, 94.64) * mm, "end": v(-221.6, 94.64) * mm});
            skLineSegment(sketch, "E634.MirrorCS", {"start": v(-354.67, 94.64) * mm, "end": v(-354.43, 31.81) * mm});
            skLineSegment(sketch, "E635.MirrorCS", {"start": v(-258.9, 100.89) * mm, "end": v(-258.9, 75.88) * mm});
            skCircle(sketch, "E636.MirrorC", {"center": v(-191.06, -61.2) * mm, "radius": 10.77 * mm});
            skLineSegment(sketch, "E637.MirrorCS", {"start": v(-264.66, 79.48) * mm, "end": v(-264.66, 100.89) * mm});
            skLineSegment(sketch, "E638.MirrorCS", {"start": v(-177.11, 47.98) * mm, "end": v(-177.11, 3) * mm});
            skLineSegment(sketch, "E639.MirrorCS", {"start": v(-314.01, -8.78) * mm, "end": v(-298.18, -8.78) * mm});
            skArc(sketch, "E640.MirrorCS", {"start": v(-377.51, 8.78) * mm, "mid": v(-369.02, 23.35) * mm, "end": v(-354.43, 31.82) * mm});
            skArc(sketch, "E641.MirrorCS", {"start": v(-262.26, 8.78) * mm, "mid": v(-253.77, 23.35) * mm, "end": v(-239.18, 31.82) * mm});
            skLineSegment(sketch, "E642.MirrorCS", {"start": v(-311.6, -79.48) * mm, "end": v(-311.6, -100.89) * mm});
            skLineSegment(sketch, "E643.MirrorCS", {"start": v(-374.14, -27.02) * mm, "end": v(-374.14, -45.33) * mm});
            skArc(sketch, "E644.MirrorCS", {"start": v(-283.9, 47.98) * mm, "mid": v(-274.78, 42.6) * mm, "end": v(-264.19, 42.87) * mm});
            skCircle(sketch, "E645.MirrorC", {"center": v(-306.32, -61.2) * mm, "radius": 10.77 * mm});
            skLineSegment(sketch, "E646.MirrorCS", {"start": v(-198.76, 8.78) * mm, "end": v(-182.93, 8.78) * mm});
            skArc(sketch, "E647.MirrorCS", {"start": v(-258.88, 45.33) * mm, "mid": v(-251.1, 56.84) * mm, "end": v(-253.03, 70.59) * mm});
            skLineSegment(sketch, "E648.MirrorCS", {"start": v(-239.41, 94.64) * mm, "end": v(-239.18, 31.81) * mm});
            skLineSegment(sketch, "E649.MirrorCS", {"start": v(-317.38, -100.89) * mm, "end": v(-342.15, -100.89) * mm});
            skLineSegment(sketch, "E650.MirrorCS", {"start": v(-398.2, -100.89) * mm, "end": v(-379.92, -100.89) * mm});
            skLineSegment(sketch, "E651.MirrorCS", {"start": v(-379.44, -42.87) * mm, "end": v(-379.44, -19.6) * mm});
            skLineSegment(sketch, "E652.MirrorCS", {"start": v(-298.18, -37.04) * mm, "end": v(-298.18, -8.78) * mm});
            skLineSegment(sketch, "E653.MirrorCS", {"start": v(-298.18, 37.04) * mm, "end": v(-298.18, 8.78) * mm});
            skLineSegment(sketch, "E654.MirrorCS", {"start": v(-283.9, -47.98) * mm, "end": v(-283.9, -3) * mm});
            skLineSegment(sketch, "E655.MirrorCS", {"start": v(-342.15, 26.62) * mm, "end": v(-342.15, 100.89) * mm});
            skLineSegment(sketch, "E656.MirrorCS", {"start": v(-374.14, 27.02) * mm, "end": v(-374.14, 45.33) * mm});
            skLineSegment(sketch, "E657.MirrorCS", {"start": v(-257.16, -3) * mm, "end": v(-283.9, -3) * mm});
            skArc(sketch, "E658.MirrorCS", {"start": v(-226.9, -26.62) * mm, "mid": v(-211.32, -18.77) * mm, "end": v(-203.86, -3) * mm});
            skLineSegment(sketch, "E659.MirrorCS", {"start": v(-385.93, 19.6) * mm, "end": v(-385.93, 35.72) * mm});
            skLineSegment(sketch, "E660.MirrorCS", {"start": v(-258.9, -100.89) * mm, "end": v(-258.9, -75.88) * mm});
            skLineSegment(sketch, "E661.MirrorCS", {"start": v(-292.37, 47.98) * mm, "end": v(-292.37, 3) * mm});
            skLineSegment(sketch, "E662.MirrorCS", {"start": v(-293.33, -75.12) * mm, "end": v(-293.33, -100.89) * mm});
            skArc(sketch, "E663.MirrorCS", {"start": v(-360.76, 36.2) * mm, "mid": v(-367.93, 32.32) * mm, "end": v(-374.14, 27.02) * mm});
            skLineSegment(sketch, "E664.MirrorCS", {"start": v(-258.9, -100.89) * mm, "end": v(-234.12, -100.89) * mm});
            skArc(sketch, "E665.MirrorCS", {"start": v(-349.38, 26.62) * mm, "mid": v(-364.96, 18.77) * mm, "end": v(-372.42, 3) * mm});
            skLineSegment(sketch, "E666.MirrorCS", {"start": v(-215.5, -70.59) * mm, "end": v(-215.5, -36.2) * mm});
            skLineSegment(sketch, "E667.MirrorCS", {"start": v(-234.12, 26.62) * mm, "end": v(-234.12, 100.89) * mm});
            skLineSegment(sketch, "E668.MirrorCS", {"start": v(-264.19, -42.87) * mm, "end": v(-264.19, -19.6) * mm});
            skArc(sketch, "E669.MirrorCS", {"start": v(-198.76, 8.78) * mm, "mid": v(-207.25, 23.35) * mm, "end": v(-221.84, 31.82) * mm});
            skLineSegment(sketch, "E670.MirrorCS", {"start": v(-203.86, -3) * mm, "end": v(-177.11, -3) * mm});
            skArc(sketch, "E671.MirrorCS", {"start": v(-215.5, 36.2) * mm, "mid": v(-208.34, 32.32) * mm, "end": v(-202.14, 27.02) * mm});
            skArc(sketch, "E672.MirrorCS", {"start": v(-226.9, 26.62) * mm, "mid": v(-211.32, 18.77) * mm, "end": v(-203.86, 3) * mm});
            skLineSegment(sketch, "E673.MirrorCS", {"start": v(-293.33, 75.12) * mm, "end": v(-293.33, 100.89) * mm});
            skArc(sketch, "E674.MirrorCS", {"start": v(-317.4, 45.33) * mm, "mid": v(-325.17, 56.84) * mm, "end": v(-323.25, 70.59) * mm});
            skLineSegment(sketch, "E675.MirrorCS", {"start": v(-264.19, 42.87) * mm, "end": v(-264.19, 19.6) * mm});
            skLineSegment(sketch, "E676.MirrorCS", {"start": v(-374.15, 100.89) * mm, "end": v(-349.38, 100.89) * mm});
            skLineSegment(sketch, "E677.MirrorCS", {"start": v(-226.9, -26.62) * mm, "end": v(-226.9, -100.89) * mm});
            skLineSegment(sketch, "E678.MirrorCS", {"start": v(-354.67, -94.64) * mm, "end": v(-354.43, -31.81) * mm});
            skArc(sketch, "E679.MirrorCS", {"start": v(-264.66, -79.48) * mm, "mid": v(-274.38, -79.71) * mm, "end": v(-282.94, -75.12) * mm});
            skLineSegment(sketch, "E680.MirrorCS", {"start": v(-317.4, 27.02) * mm, "end": v(-317.4, 45.33) * mm});
            skArc(sketch, "E681.MirrorCS", {"start": v(-314.01, -8.78) * mm, "mid": v(-322.5, -23.35) * mm, "end": v(-337.1, -31.82) * mm});
            skArc(sketch, "E682.MirrorCS", {"start": v(-342.15, 26.62) * mm, "mid": v(-326.57, 18.77) * mm, "end": v(-319.11, 3) * mm});
            skArc(sketch, "E683.MirrorCS", {"start": v(-198.76, -8.78) * mm, "mid": v(-207.25, -23.35) * mm, "end": v(-221.84, -31.82) * mm});
            skLineSegment(sketch, "E684.MirrorCS", {"start": v(-221.6, 94.64) * mm, "end": v(-221.84, 31.81) * mm});
            skArc(sketch, "E685.MirrorCS", {"start": v(-374.14, -45.33) * mm, "mid": v(-366.36, -56.84) * mm, "end": v(-368.28, -70.59) * mm});
            skLineSegment(sketch, "E686.MirrorCS", {"start": v(-262.26, 8.78) * mm, "end": v(-278.1, 8.78) * mm});
            skCircle(sketch, "E687.MirrorC", {"center": v(-269.96, 61.2) * mm, "radius": 10.77 * mm});
            skLineSegment(sketch, "E688.MirrorCS", {"start": v(-282.94, 75.12) * mm, "end": v(-282.94, 100.89) * mm});
            skCircle(sketch, "E689.MirrorC", {"center": v(-385.2, -61.2) * mm, "radius": 10.77 * mm});
            skArc(sketch, "E690.MirrorCS", {"start": v(-202.14, 45.33) * mm, "mid": v(-209.92, 56.84) * mm, "end": v(-208, 70.59) * mm});
            skArc(sketch, "E691.MirrorCS", {"start": v(-292.37, 47.98) * mm, "mid": v(-301.5, 42.6) * mm, "end": v(-312.09, 42.87) * mm});
            skLineSegment(sketch, "E692.MirrorCS", {"start": v(-221.6, -94.64) * mm, "end": v(-221.84, -31.81) * mm});
            skLineSegment(sketch, "E693.MirrorCS", {"start": v(-312.09, -42.87) * mm, "end": v(-312.09, -19.6) * mm});
            skLineSegment(sketch, "E694.MirrorCS", {"start": v(-372.42, 3) * mm, "end": v(-399.16, 3) * mm});
            skArc(sketch, "E695.MirrorCS", {"start": v(-245.5, -36.2) * mm, "mid": v(-252.68, -32.32) * mm, "end": v(-258.88, -27.02) * mm});
            skLineSegment(sketch, "E696.MirrorCS", {"start": v(-293.33, -100.89) * mm, "end": v(-311.6, -100.89) * mm});
            skLineSegment(sketch, "E697.MirrorCS", {"start": v(-196.83, 42.87) * mm, "end": v(-196.83, 19.6) * mm});
            skLineSegment(sketch, "E698.MirrorCS", {"start": v(-398.2, 75.12) * mm, "end": v(-398.2, 100.89) * mm});
            skLineSegment(sketch, "E699.MirrorCS", {"start": v(-311.6, 79.48) * mm, "end": v(-311.6, 100.89) * mm});
            skLineSegment(sketch, "E700.MirrorCS", {"start": v(-182.93, 37.04) * mm, "end": v(-182.93, 8.78) * mm});
            skArc(sketch, "E701.MirrorCS", {"start": v(-245.5, 36.2) * mm, "mid": v(-252.68, 32.32) * mm, "end": v(-258.88, 27.02) * mm});
            skLineSegment(sketch, "E702.MirrorCS", {"start": v(-372.42, -3) * mm, "end": v(-399.16, -3) * mm});
            skArc(sketch, "E703.MirrorCS", {"start": v(-234.12, 26.62) * mm, "mid": v(-249.7, 18.77) * mm, "end": v(-257.16, 3) * mm});
            skLineSegment(sketch, "E704.MirrorCS", {"start": v(-282.94, 100.89) * mm, "end": v(-264.66, 100.89) * mm});
            skArc(sketch, "E705.MirrorCS", {"start": v(-311.6, -79.48) * mm, "mid": v(-301.9, -79.71) * mm, "end": v(-293.33, -75.12) * mm});
            skLineSegment(sketch, "E706.MirrorCS", {"start": v(-239.41, -94.64) * mm, "end": v(-239.18, -31.81) * mm});
            skLineSegment(sketch, "E707.MirrorCS", {"start": v(-305.6, -19.6) * mm, "end": v(-305.6, -35.72) * mm});
            skLineSegment(sketch, "E708.MirrorCS", {"start": v(-196.35, 79.48) * mm, "end": v(-196.35, 100.89) * mm});
            skCircle(sketch, "E709.MirrorC", {"center": v(-269.96, -61.2) * mm, "radius": 10.77 * mm});
            skLineSegment(sketch, "E710.MirrorCS", {"start": v(-196.83, -42.87) * mm, "end": v(-196.83, -19.6) * mm});
            skLineSegment(sketch, "E711.MirrorCS", {"start": v(-278.1, -37.04) * mm, "end": v(-278.1, -8.78) * mm});
            skLineSegment(sketch, "E712.MirrorCS", {"start": v(-399.16, 47.98) * mm, "end": v(-399.16, 3) * mm});
            skArc(sketch, "E713.MirrorCS", {"start": v(-292.37, -47.98) * mm, "mid": v(-301.5, -42.6) * mm, "end": v(-312.09, -42.87) * mm});
            skLineSegment(sketch, "E714.MirrorCS", {"start": v(-196.35, -79.48) * mm, "end": v(-196.35, -100.89) * mm});
            skLineSegment(sketch, "E715.MirrorCS", {"start": v(-342.15, -26.62) * mm, "end": v(-342.15, -100.89) * mm});
            skLineSegment(sketch, "E716.MirrorCS", {"start": v(-336.86, -94.64) * mm, "end": v(-337.1, -31.81) * mm});
            skLineSegment(sketch, "E717.MirrorCS", {"start": v(-393.35, -37.04) * mm, "end": v(-393.35, -8.78) * mm});
            skLineSegment(sketch, "E718.MirrorCS", {"start": v(-270.68, -19.6) * mm, "end": v(-270.68, -35.72) * mm});
            skLineSegment(sketch, "E719.MirrorCS", {"start": v(-253.62, -94.64) * mm, "end": v(-239.41, -94.64) * mm});
            skLineSegment(sketch, "E720.MirrorCS", {"start": v(-178.08, 100.89) * mm, "end": v(-196.35, 100.89) * mm});
            skArc(sketch, "E721.MirrorCS", {"start": v(-202.14, -45.33) * mm, "mid": v(-209.92, -56.84) * mm, "end": v(-208, -70.59) * mm});
            skLineSegment(sketch, "E722.MirrorCS", {"start": v(-226.9, 26.62) * mm, "end": v(-226.9, 100.89) * mm});
            skArc(sketch, "E723.MirrorCS", {"start": v(-234.12, -26.62) * mm, "mid": v(-249.7, -18.77) * mm, "end": v(-257.16, -3) * mm});
            skLineSegment(sketch, "E724.MirrorCS", {"start": v(-282.94, -75.12) * mm, "end": v(-282.94, -100.89) * mm});
            skLineSegment(sketch, "E725.MirrorCS", {"start": v(-258.9, 100.89) * mm, "end": v(-234.12, 100.89) * mm});
            skLineSegment(sketch, "E726.MirrorCS", {"start": v(-207.4, -94.64) * mm, "end": v(-221.6, -94.64) * mm});
            skArc(sketch, "E727.MirrorCS", {"start": v(-330.76, 36.2) * mm, "mid": v(-323.6, 32.32) * mm, "end": v(-317.4, 27.02) * mm});
            skLineSegment(sketch, "E728.MirrorCS", {"start": v(-314.01, 8.78) * mm, "end": v(-298.18, 8.78) * mm});
            skLineSegment(sketch, "E729.MirrorCS", {"start": v(-385.93, -19.6) * mm, "end": v(-385.93, -35.72) * mm});
            skCircle(sketch, "E730.MirrorC", {"center": v(-191.06, 61.2) * mm, "radius": 10.77 * mm});
            skArc(sketch, "E731.MirrorCS", {"start": v(-360.76, -36.2) * mm, "mid": v(-367.93, -32.32) * mm, "end": v(-374.14, -27.02) * mm});
            skLineSegment(sketch, "E732.MirrorCS", {"start": v(-377.51, -8.78) * mm, "end": v(-393.35, -8.78) * mm});
            skLineSegment(sketch, "E733.MirrorCS", {"start": v(-360.76, -70.59) * mm, "end": v(-360.76, -36.2) * mm});
            skLineSegment(sketch, "E734.MirrorCS", {"start": v(-399.16, -47.98) * mm, "end": v(-399.16, -3) * mm});
            skCircle(sketch, "E735.MirrorC", {"center": v(-306.32, 61.2) * mm, "radius": 10.77 * mm});
            skLineSegment(sketch, "E736.MirrorCS", {"start": v(-178.08, -75.12) * mm, "end": v(-178.08, -100.89) * mm});
            skLineSegment(sketch, "E737.MirrorCS", {"start": v(-283.9, 47.98) * mm, "end": v(-283.9, 3) * mm});
            skLineSegment(sketch, "E738.MirrorCS", {"start": v(-253.62, 94.64) * mm, "end": v(-239.41, 94.64) * mm});
            skLineSegment(sketch, "E739.MirrorCS", {"start": v(-322.65, -94.64) * mm, "end": v(-336.86, -94.64) * mm});
            skLineSegment(sketch, "E740.MirrorCS", {"start": v(-278.1, 37.04) * mm, "end": v(-278.1, 8.78) * mm});
            skLineSegment(sketch, "E741.MirrorCS", {"start": v(-393.35, 37.04) * mm, "end": v(-393.35, 8.78) * mm});
            skArc(sketch, "E742.MirrorCS", {"start": v(-317.4, -45.33) * mm, "mid": v(-325.17, -56.84) * mm, "end": v(-323.25, -70.59) * mm});
            skArc(sketch, "E743.MirrorCS", {"start": v(-258.88, -45.33) * mm, "mid": v(-251.1, -56.84) * mm, "end": v(-253.03, -70.59) * mm});
            skLineSegment(sketch, "E744.MirrorCS", {"start": v(-262.26, -8.78) * mm, "end": v(-278.1, -8.78) * mm});
            skArc(sketch, "E745.MirrorCS", {"start": v(-399.16, -47.98) * mm, "mid": v(-390.03, -42.6) * mm, "end": v(-379.44, -42.87) * mm});
            skLineSegment(sketch, "E746.MirrorCS", {"start": v(-398.2, -75.12) * mm, "end": v(-398.2, -100.89) * mm});
            skArc(sketch, "E747.MirrorCS", {"start": v(-349.38, -26.62) * mm, "mid": v(-364.96, -18.77) * mm, "end": v(-372.42, -3) * mm});
            skLineSegment(sketch, "E748.MirrorCS", {"start": v(-330.76, 70.59) * mm, "end": v(-330.76, 36.2) * mm});
            skLineSegment(sketch, "E749.MirrorCS", {"start": v(-202.13, -100.89) * mm, "end": v(-226.9, -100.89) * mm});
            skArc(sketch, "E750.MirrorCS", {"start": v(-379.92, -79.48) * mm, "mid": v(-389.63, -79.71) * mm, "end": v(-398.2, -75.12) * mm});
            skLineSegment(sketch, "E751.MirrorCS", {"start": v(-319.11, 3) * mm, "end": v(-292.37, 3) * mm});
            skLineSegment(sketch, "E752.MirrorCS", {"start": v(-330.76, -70.59) * mm, "end": v(-330.76, -36.2) * mm});
            skLineSegment(sketch, "E753.MirrorCS", {"start": v(-317.4, -27.02) * mm, "end": v(-317.4, -45.33) * mm});
            skArc(sketch, "E754.MirrorCS", {"start": v(-399.16, 47.98) * mm, "mid": v(-390.03, 42.6) * mm, "end": v(-379.44, 42.87) * mm});
            skLineSegment(sketch, "E755.MirrorCS", {"start": v(-182.93, -37.04) * mm, "end": v(-182.93, -8.78) * mm});
            skArc(sketch, "E756.MirrorCS", {"start": v(-377.51, -8.78) * mm, "mid": v(-369.02, -23.35) * mm, "end": v(-354.43, -31.82) * mm});
            skLineSegment(sketch, "E757.MirrorCS", {"start": v(-257.16, 3) * mm, "end": v(-283.9, 3) * mm});
            skLineSegment(sketch, "E758.MirrorCS", {"start": v(-349.38, 26.62) * mm, "end": v(-349.38, 100.89) * mm});
            skCircle(sketch, "E759.MirrorC", {"center": v(-345.76, 0) * mm, "radius": 20.2 * mm});
            skCircle(sketch, "E760.MirrorC", {"center": v(-230.5, 0) * mm, "radius": 20.2 * mm});
            skSolve(sketch);
        }
        {
            var Q0;
            Q0=makeQuery(id+"F0.imprint","IMPRINT",FACE,{"disambiguationData":[TD([[makeQuery(id+"F0.imprint","IMPRINT",EDGE,{"derivedFrom":sQuery(id+"F0.wireOp",EDGE,"E147.MirrorCS")}),1.0]])]});
            var Q1;
            Q1=makeQuery(id+"F0.imprint","IMPRINT",FACE,{"disambiguationData":[TD([[makeQuery(id+"F0.imprint","IMPRINT",EDGE,{"derivedFrom":sQuery(id+"F0.wireOp",EDGE,"E578.MirrorCS")}),-1.0]])]});
            var Q2;
            Q2=makeQuery(id+"F0.imprint","IMPRINT",FACE,{"disambiguationData":[TD([[makeQuery(id+"F0.imprint","IMPRINT",EDGE,{"derivedFrom":sQuery(id+"F0.wireOp",EDGE,"E519.MirrorCS")}),-1.0]])]});
            var Q3;
            Q3=makeQuery(id+"F0.imprint","IMPRINT",FACE,{"disambiguationData":[TD([[makeQuery(id+"F0.imprint","IMPRINT",EDGE,{"derivedFrom":sQuery(id+"F0.wireOp",EDGE,"E72.MirrorCS")}),1.0]])]});
            var Q4;
            Q4=makeQuery(id+"F0.imprint","IMPRINT",FACE,{"disambiguationData":[TD([[makeQuery(id+"F0.imprint","IMPRINT",EDGE,{"derivedFrom":sQuery(id+"F0.wireOp",EDGE,"E268.MirrorCS")}),1.0]])]});
            var Q5;
            Q5=makeQuery(id+"F0.imprint","IMPRINT",FACE,{"disambiguationData":[TD([[makeQuery(id+"F0.imprint","IMPRINT",EDGE,{"derivedFrom":sQuery(id+"F0.wireOp",EDGE,"E265.MirrorCS")}),-1.0]])]});
            extrude(context, id + "F1", {"entities" : qUnion([Q0, Q1, Q2, Q3, Q4, Q5]), "depth" : 1.5 * mm, "offsetDistance" : 25 * mm});
        }
    });
